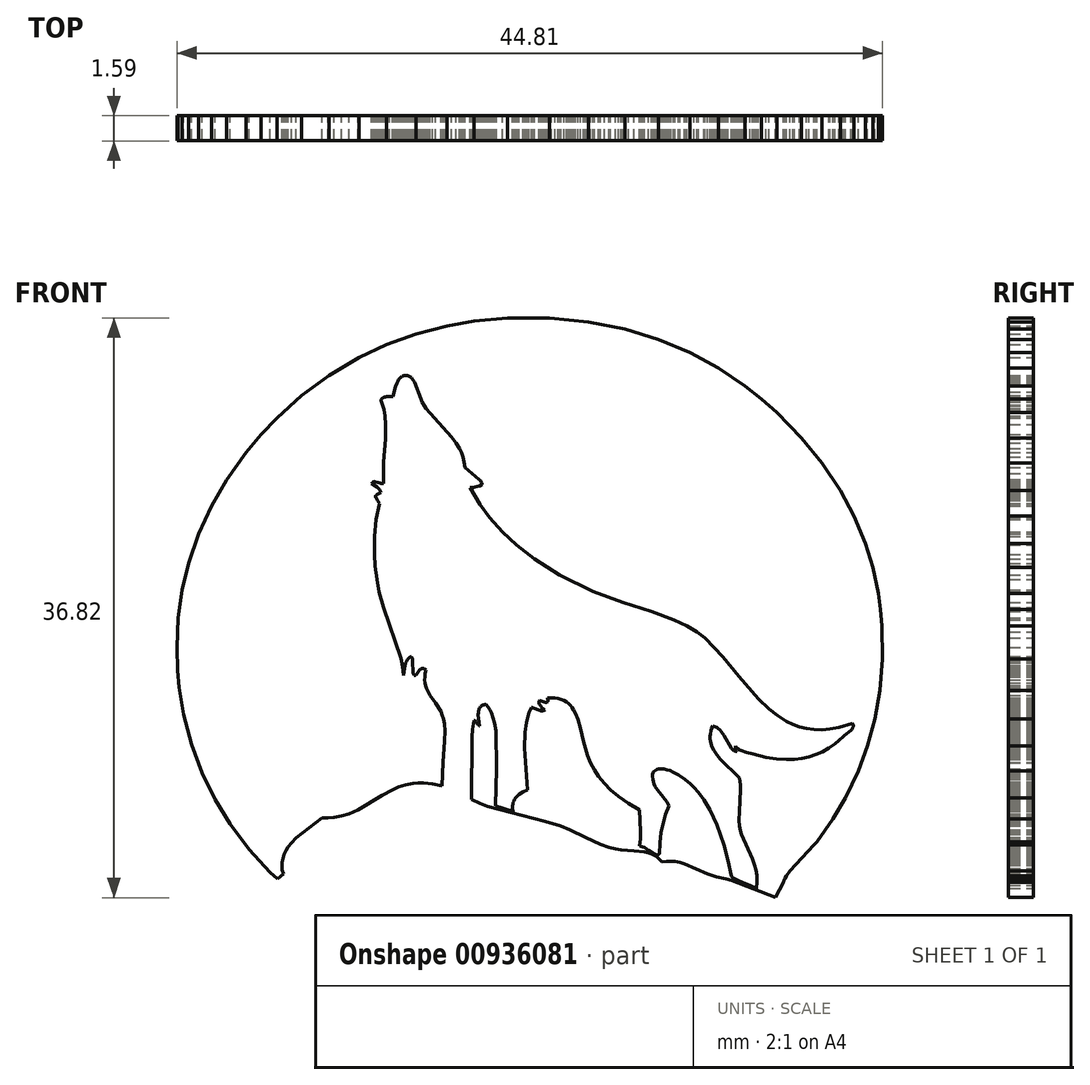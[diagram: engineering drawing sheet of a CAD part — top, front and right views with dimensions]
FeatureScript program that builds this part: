
annotation { "Feature Type Name" : "Feature", "Feature Type Description" : "" }
export const myFeature = defineFeature(function(context is Context, id is Id, definition is map)
    precondition{}
    {
        {
            var Q0;
            Q0=qCreatedBy(makeId("Front.planeOp"),FACE);
            var sketch = newSketch(context, id + "F0", { "sketchPlane" : qUnion([Q0])});
            skLineSegment(sketch, "E0", {"start": v(-25.4, -24.26) * mm, "end": v(-25.3, -24.48) * mm});
            skLineSegment(sketch, "E1", {"start": v(-25.3, -24.48) * mm, "end": v(-25.21, -24.65) * mm});
            skLineSegment(sketch, "E2", {"start": v(-25.21, -24.65) * mm, "end": v(-25.12, -24.8) * mm});
            skLineSegment(sketch, "E3", {"start": v(-25.12, -24.8) * mm, "end": v(-25.03, -24.9) * mm});
            skLineSegment(sketch, "E4", {"start": v(-25.03, -24.9) * mm, "end": v(-24.93, -25) * mm});
            skLineSegment(sketch, "E5", {"start": v(-24.93, -25) * mm, "end": v(-24.82, -25.08) * mm});
            skLineSegment(sketch, "E6", {"start": v(-24.82, -25.08) * mm, "end": v(-24.7, -25.16) * mm});
            skLineSegment(sketch, "E7", {"start": v(-24.7, -25.16) * mm, "end": v(-24.6, -25.21) * mm});
            skLineSegment(sketch, "E8", {"start": v(-24.6, -25.21) * mm, "end": v(-24.47, -25.27) * mm});
            skLineSegment(sketch, "E9", {"start": v(-24.47, -25.27) * mm, "end": v(-14.22, -25.27) * mm});
            skLineSegment(sketch, "E10", {"start": v(-14.22, -25.27) * mm, "end": v(-16.34, -23.58) * mm});
            skLineSegment(sketch, "E11", {"start": v(-16.34, -23.58) * mm, "end": v(-17.75, -22.6) * mm});
            skLineSegment(sketch, "E12", {"start": v(-17.75, -22.6) * mm, "end": v(-17.95, -22.4) * mm});
            skLineSegment(sketch, "E13", {"start": v(-17.95, -22.4) * mm, "end": v(-18.06, -22.27) * mm});
            skLineSegment(sketch, "E14", {"start": v(-18.06, -22.27) * mm, "end": v(-18.14, -22.14) * mm});
            skLineSegment(sketch, "E15", {"start": v(-18.14, -22.14) * mm, "end": v(-18.21, -22) * mm});
            skLineSegment(sketch, "E16", {"start": v(-18.21, -22) * mm, "end": v(-18.25, -21.91) * mm});
            skLineSegment(sketch, "E17", {"start": v(-18.25, -21.91) * mm, "end": v(-18.27, -21.82) * mm});
            skLineSegment(sketch, "E18", {"start": v(-18.27, -21.82) * mm, "end": v(-18.29, -21.72) * mm});
            skLineSegment(sketch, "E19", {"start": v(-18.29, -21.72) * mm, "end": v(-18.3, -21.66) * mm});
            skLineSegment(sketch, "E20", {"start": v(-18.3, -21.66) * mm, "end": v(-18.29, -21.58) * mm});
            skLineSegment(sketch, "E21", {"start": v(-18.29, -21.58) * mm, "end": v(-18.27, -21.49) * mm});
            skLineSegment(sketch, "E22", {"start": v(-18.27, -21.49) * mm, "end": v(-18.23, -21.33) * mm});
            skLineSegment(sketch, "E23", {"start": v(-18.23, -21.33) * mm, "end": v(-17.9, -20.37) * mm});
            skLineSegment(sketch, "E24", {"start": v(-17.9, -20.37) * mm, "end": v(-17.87, -20.24) * mm});
            skLineSegment(sketch, "E25", {"start": v(-17.87, -20.24) * mm, "end": v(-17.87, -20.17) * mm});
            skLineSegment(sketch, "E26", {"start": v(-17.87, -20.17) * mm, "end": v(-17.86, -20.1) * mm});
            skLineSegment(sketch, "E27", {"start": v(-17.86, -20.1) * mm, "end": v(-17.87, -20.02) * mm});
            skLineSegment(sketch, "E28", {"start": v(-17.87, -20.02) * mm, "end": v(-17.9, -19.9) * mm});
            skLineSegment(sketch, "E29", {"start": v(-17.9, -19.9) * mm, "end": v(-17.93, -19.76) * mm});
            skLineSegment(sketch, "E30", {"start": v(-17.93, -19.76) * mm, "end": v(-18, -19.6) * mm});
            skLineSegment(sketch, "E31", {"start": v(-18, -19.6) * mm, "end": v(-18.16, -19.28) * mm});
            skLineSegment(sketch, "E32", {"start": v(-18.16, -19.28) * mm, "end": v(-18.57, -18.53) * mm});
            skLineSegment(sketch, "E33", {"start": v(-18.57, -18.53) * mm, "end": v(-18.64, -18.35) * mm});
            skLineSegment(sketch, "E34", {"start": v(-18.64, -18.35) * mm, "end": v(-18.68, -18.22) * mm});
            skLineSegment(sketch, "E35", {"start": v(-18.68, -18.22) * mm, "end": v(-18.7, -18.08) * mm});
            skLineSegment(sketch, "E36", {"start": v(-18.7, -18.08) * mm, "end": v(-18.71, -18) * mm});
            skLineSegment(sketch, "E37", {"start": v(-18.71, -18) * mm, "end": v(-18.71, -17.9) * mm});
            skLineSegment(sketch, "E38", {"start": v(-18.71, -17.9) * mm, "end": v(-18.7, -17.78) * mm});
            skLineSegment(sketch, "E39", {"start": v(-18.7, -17.78) * mm, "end": v(-18.66, -17.65) * mm});
            skLineSegment(sketch, "E40", {"start": v(-18.66, -17.65) * mm, "end": v(-18.6, -17.54) * mm});
            skLineSegment(sketch, "E41", {"start": v(-18.6, -17.54) * mm, "end": v(-18.54, -17.42) * mm});
            skLineSegment(sketch, "E42", {"start": v(-18.54, -17.42) * mm, "end": v(-18.46, -17.31) * mm});
            skLineSegment(sketch, "E43", {"start": v(-18.46, -17.31) * mm, "end": v(-18.32, -17.15) * mm});
            skLineSegment(sketch, "E44", {"start": v(-18.32, -17.15) * mm, "end": v(-18.1, -16.95) * mm});
            skLineSegment(sketch, "E45", {"start": v(-18.1, -16.95) * mm, "end": v(-17.67, -16.63) * mm});
            skLineSegment(sketch, "E46", {"start": v(-17.67, -16.63) * mm, "end": v(-16.85, -16.04) * mm});
            skLineSegment(sketch, "E47", {"start": v(-16.85, -16.04) * mm, "end": v(-16.72, -15.92) * mm});
            skLineSegment(sketch, "E48", {"start": v(-16.72, -15.92) * mm, "end": v(-16.64, -15.84) * mm});
            skLineSegment(sketch, "E49", {"start": v(-16.64, -15.84) * mm, "end": v(-16.59, -15.75) * mm});
            skLineSegment(sketch, "E50", {"start": v(-16.59, -15.75) * mm, "end": v(-16.54, -15.67) * mm});
            skLineSegment(sketch, "E51", {"start": v(-16.54, -15.67) * mm, "end": v(-16.53, -15.62) * mm});
            skLineSegment(sketch, "E52", {"start": v(-16.53, -15.62) * mm, "end": v(-16.52, -15.58) * mm});
            skLineSegment(sketch, "E53", {"start": v(-16.52, -15.58) * mm, "end": v(-16.51, -15.54) * mm});
            skLineSegment(sketch, "E54", {"start": v(-16.51, -15.54) * mm, "end": v(-16.5, -15.5) * mm});
            skLineSegment(sketch, "E55", {"start": v(-16.5, -15.5) * mm, "end": v(-16.51, -15.48) * mm});
            skLineSegment(sketch, "E56", {"start": v(-16.51, -15.48) * mm, "end": v(-16.52, -15.43) * mm});
            skLineSegment(sketch, "E57", {"start": v(-16.52, -15.43) * mm, "end": v(-16.54, -15.37) * mm});
            skLineSegment(sketch, "E58", {"start": v(-16.54, -15.37) * mm, "end": v(-16.57, -15.3) * mm});
            skLineSegment(sketch, "E59", {"start": v(-16.57, -15.3) * mm, "end": v(-16.62, -15.21) * mm});
            skLineSegment(sketch, "E60", {"start": v(-16.62, -15.21) * mm, "end": v(-16.72, -15.08) * mm});
            skLineSegment(sketch, "E61", {"start": v(-16.72, -15.08) * mm, "end": v(-16.9, -14.88) * mm});
            skLineSegment(sketch, "E62", {"start": v(-16.9, -14.88) * mm, "end": v(-17.4, -14.42) * mm});
            skLineSegment(sketch, "E63", {"start": v(-17.4, -14.42) * mm, "end": v(-17.86, -14.01) * mm});
            skLineSegment(sketch, "E64", {"start": v(-17.86, -14.01) * mm, "end": v(-19.2, -12.55) * mm});
            skLineSegment(sketch, "E65", {"start": v(-19.2, -12.55) * mm, "end": v(-20.43, -10.91) * mm});
            skLineSegment(sketch, "E66", {"start": v(-20.43, -10.91) * mm, "end": v(-21.37, -9.37) * mm});
            skLineSegment(sketch, "E67", {"start": v(-21.37, -9.37) * mm, "end": v(-22.2, -7.7) * mm});
            skLineSegment(sketch, "E68", {"start": v(-22.2, -7.7) * mm, "end": v(-22.87, -5.9) * mm});
            skLineSegment(sketch, "E69", {"start": v(-22.87, -5.9) * mm, "end": v(-23.37, -3.96) * mm});
            skLineSegment(sketch, "E70", {"start": v(-23.37, -3.96) * mm, "end": v(-23.65, -2.25) * mm});
            skLineSegment(sketch, "E71", {"start": v(-23.65, -2.25) * mm, "end": v(-23.75, -1.18) * mm});
            skLineSegment(sketch, "E72", {"start": v(-23.75, -1.18) * mm, "end": v(-23.8, 0.3) * mm});
            skLineSegment(sketch, "E73", {"start": v(-23.8, 0.3) * mm, "end": v(-23.7, 2.16) * mm});
            skLineSegment(sketch, "E74", {"start": v(-23.7, 2.16) * mm, "end": v(-23.44, 3.93) * mm});
            skLineSegment(sketch, "E75", {"start": v(-23.44, 3.93) * mm, "end": v(-23.04, 5.6) * mm});
            skLineSegment(sketch, "E76", {"start": v(-23.04, 5.6) * mm, "end": v(-22.4, 7.5) * mm});
            skLineSegment(sketch, "E77", {"start": v(-22.4, 7.5) * mm, "end": v(-21.58, 9.27) * mm});
            skLineSegment(sketch, "E78", {"start": v(-21.58, 9.27) * mm, "end": v(-20.64, 10.9) * mm});
            skLineSegment(sketch, "E79", {"start": v(-20.64, 10.9) * mm, "end": v(-19.4, 12.66) * mm});
            skLineSegment(sketch, "E80", {"start": v(-19.4, 12.66) * mm, "end": v(-18.44, 13.8) * mm});
            skLineSegment(sketch, "E81", {"start": v(-18.44, 13.8) * mm, "end": v(-17.44, 14.86) * mm});
            skLineSegment(sketch, "E82", {"start": v(-17.44, 14.86) * mm, "end": v(-15.87, 16.28) * mm});
            skLineSegment(sketch, "E83", {"start": v(-15.87, 16.28) * mm, "end": v(-14.13, 17.56) * mm});
            skLineSegment(sketch, "E84", {"start": v(-14.13, 17.56) * mm, "end": v(-12.22, 18.69) * mm});
            skLineSegment(sketch, "E85", {"start": v(-12.22, 18.69) * mm, "end": v(-10.46, 19.51) * mm});
            skLineSegment(sketch, "E86", {"start": v(-10.46, 19.51) * mm, "end": v(-8.6, 20.2) * mm});
            skLineSegment(sketch, "E87", {"start": v(-8.6, 20.2) * mm, "end": v(-6.63, 20.71) * mm});
            skLineSegment(sketch, "E88", {"start": v(-6.63, 20.71) * mm, "end": v(-4.92, 21.02) * mm});
            skLineSegment(sketch, "E89", {"start": v(-4.92, 21.02) * mm, "end": v(-2.8, 21.2) * mm});
            skLineSegment(sketch, "E90", {"start": v(-2.8, 21.2) * mm, "end": v(-0.13, 21.2) * mm});
            skLineSegment(sketch, "E91", {"start": v(-0.13, 21.2) * mm, "end": v(2.36, 20.96) * mm});
            skLineSegment(sketch, "E92", {"start": v(2.36, 20.96) * mm, "end": v(4.67, 20.5) * mm});
            skLineSegment(sketch, "E93", {"start": v(4.67, 20.5) * mm, "end": v(6.81, 19.85) * mm});
            skLineSegment(sketch, "E94", {"start": v(6.81, 19.85) * mm, "end": v(8.79, 19.01) * mm});
            skLineSegment(sketch, "E95", {"start": v(8.79, 19.01) * mm, "end": v(10.61, 18.02) * mm});
            skLineSegment(sketch, "E96", {"start": v(10.61, 18.02) * mm, "end": v(12.3, 16.89) * mm});
            skLineSegment(sketch, "E97", {"start": v(12.3, 16.89) * mm, "end": v(13.33, 16.07) * mm});
            skLineSegment(sketch, "E98", {"start": v(13.33, 16.07) * mm, "end": v(14.3, 15.2) * mm});
            skLineSegment(sketch, "E99", {"start": v(14.3, 15.2) * mm, "end": v(15.89, 13.58) * mm});
            skLineSegment(sketch, "E100", {"start": v(15.89, 13.58) * mm, "end": v(17.18, 12) * mm});
            skLineSegment(sketch, "E101", {"start": v(17.18, 12) * mm, "end": v(18.34, 10.26) * mm});
            skLineSegment(sketch, "E102", {"start": v(18.34, 10.26) * mm, "end": v(19.21, 8.64) * mm});
            skLineSegment(sketch, "E103", {"start": v(19.21, 8.64) * mm, "end": v(19.94, 6.9) * mm});
            skLineSegment(sketch, "E104", {"start": v(19.94, 6.9) * mm, "end": v(20.42, 5.36) * mm});
            skLineSegment(sketch, "E105", {"start": v(20.42, 5.36) * mm, "end": v(20.77, 3.73) * mm});
            skLineSegment(sketch, "E106", {"start": v(20.77, 3.73) * mm, "end": v(20.9, 2.7) * mm});
            skLineSegment(sketch, "E107", {"start": v(20.9, 2.7) * mm, "end": v(21, 1.65) * mm});
            skLineSegment(sketch, "E108", {"start": v(21, 1.65) * mm, "end": v(21.02, -0.46) * mm});
            skLineSegment(sketch, "E109", {"start": v(21.02, -0.46) * mm, "end": v(20.87, -2.43) * mm});
            skLineSegment(sketch, "E110", {"start": v(20.87, -2.43) * mm, "end": v(20.55, -4.27) * mm});
            skLineSegment(sketch, "E111", {"start": v(20.55, -4.27) * mm, "end": v(20.09, -5.98) * mm});
            skLineSegment(sketch, "E112", {"start": v(20.09, -5.98) * mm, "end": v(19.5, -7.57) * mm});
            skLineSegment(sketch, "E113", {"start": v(19.5, -7.57) * mm, "end": v(18.67, -9.27) * mm});
            skLineSegment(sketch, "E114", {"start": v(18.67, -9.27) * mm, "end": v(17.87, -10.62) * mm});
            skLineSegment(sketch, "E115", {"start": v(17.87, -10.62) * mm, "end": v(16.85, -12.07) * mm});
            skLineSegment(sketch, "E116", {"start": v(16.85, -12.07) * mm, "end": v(16.67, -12.27) * mm});
            skLineSegment(sketch, "E117", {"start": v(16.67, -12.27) * mm, "end": v(15.14, -13.9) * mm});
            skLineSegment(sketch, "E118", {"start": v(15.14, -13.9) * mm, "end": v(14.92, -14.21) * mm});
            skLineSegment(sketch, "E119", {"start": v(14.92, -14.21) * mm, "end": v(14.82, -14.4) * mm});
            skLineSegment(sketch, "E120", {"start": v(14.82, -14.4) * mm, "end": v(14.77, -14.52) * mm});
            skLineSegment(sketch, "E121", {"start": v(14.77, -14.52) * mm, "end": v(14.74, -14.63) * mm});
            skLineSegment(sketch, "E122", {"start": v(14.74, -14.63) * mm, "end": v(14.72, -14.74) * mm});
            skLineSegment(sketch, "E123", {"start": v(14.72, -14.74) * mm, "end": v(14.72, -14.85) * mm});
            skLineSegment(sketch, "E124", {"start": v(14.72, -14.85) * mm, "end": v(14.72, -14.9) * mm});
            skLineSegment(sketch, "E125", {"start": v(14.72, -14.9) * mm, "end": v(14.73, -14.94) * mm});
            skLineSegment(sketch, "E126", {"start": v(14.73, -14.94) * mm, "end": v(14.74, -14.98) * mm});
            skLineSegment(sketch, "E127", {"start": v(14.74, -14.98) * mm, "end": v(14.76, -15) * mm});
            skLineSegment(sketch, "E128", {"start": v(14.76, -15) * mm, "end": v(14.8, -15.07) * mm});
            skLineSegment(sketch, "E129", {"start": v(14.8, -15.07) * mm, "end": v(14.84, -15.12) * mm});
            skLineSegment(sketch, "E130", {"start": v(14.84, -15.12) * mm, "end": v(14.9, -15.17) * mm});
            skLineSegment(sketch, "E131", {"start": v(14.9, -15.17) * mm, "end": v(14.96, -15.23) * mm});
            skLineSegment(sketch, "E132", {"start": v(14.96, -15.23) * mm, "end": v(15.08, -15.3) * mm});
            skLineSegment(sketch, "E133", {"start": v(15.08, -15.3) * mm, "end": v(15.26, -15.39) * mm});
            skLineSegment(sketch, "E134", {"start": v(15.26, -15.39) * mm, "end": v(16.16, -15.66) * mm});
            skLineSegment(sketch, "E135", {"start": v(16.16, -15.66) * mm, "end": v(17.02, -15.88) * mm});
            skLineSegment(sketch, "E136", {"start": v(17.02, -15.88) * mm, "end": v(18.6, -16.34) * mm});
            skLineSegment(sketch, "E137", {"start": v(18.6, -16.34) * mm, "end": v(18.9, -16.48) * mm});
            skLineSegment(sketch, "E138", {"start": v(18.9, -16.48) * mm, "end": v(19.1, -16.6) * mm});
            skLineSegment(sketch, "E139", {"start": v(19.1, -16.6) * mm, "end": v(19.25, -16.7) * mm});
            skLineSegment(sketch, "E140", {"start": v(19.25, -16.7) * mm, "end": v(19.39, -16.8) * mm});
            skLineSegment(sketch, "E141", {"start": v(19.39, -16.8) * mm, "end": v(18.26, -16.72) * mm});
            skLineSegment(sketch, "E142", {"start": v(18.26, -16.72) * mm, "end": v(17.04, -16.51) * mm});
            skLineSegment(sketch, "E143", {"start": v(17.04, -16.51) * mm, "end": v(14.22, -15.6) * mm});
            skLineSegment(sketch, "E144", {"start": v(14.22, -15.6) * mm, "end": v(11.43, -14.52) * mm});
            skLineSegment(sketch, "E145", {"start": v(11.43, -14.52) * mm, "end": v(11.07, -14.42) * mm});
            skLineSegment(sketch, "E146", {"start": v(11.07, -14.42) * mm, "end": v(10.48, -14.28) * mm});
            skLineSegment(sketch, "E147", {"start": v(10.48, -14.28) * mm, "end": v(9.9, -14.1) * mm});
            skLineSegment(sketch, "E148", {"start": v(9.9, -14.1) * mm, "end": v(8.46, -13.45) * mm});
            skLineSegment(sketch, "E149", {"start": v(8.46, -13.45) * mm, "end": v(8.17, -13.37) * mm});
            skLineSegment(sketch, "E150", {"start": v(8.17, -13.37) * mm, "end": v(7.86, -13.32) * mm});
            skLineSegment(sketch, "E151", {"start": v(7.86, -13.32) * mm, "end": v(7.6, -13.3) * mm});
            skLineSegment(sketch, "E152", {"start": v(7.6, -13.3) * mm, "end": v(7.32, -13.3) * mm});
            skLineSegment(sketch, "E153", {"start": v(7.32, -13.3) * mm, "end": v(7.03, -13.34) * mm});
            skLineSegment(sketch, "E154", {"start": v(7.03, -13.34) * mm, "end": v(6.87, -13.16) * mm});
            skLineSegment(sketch, "E155", {"start": v(6.87, -13.16) * mm, "end": v(6.74, -13.06) * mm});
            skLineSegment(sketch, "E156", {"start": v(6.74, -13.06) * mm, "end": v(6.61, -12.97) * mm});
            skLineSegment(sketch, "E157", {"start": v(6.61, -12.97) * mm, "end": v(6.48, -12.9) * mm});
            skLineSegment(sketch, "E158", {"start": v(6.48, -12.9) * mm, "end": v(6.35, -12.83) * mm});
            skLineSegment(sketch, "E159", {"start": v(6.35, -12.83) * mm, "end": v(6.16, -12.76) * mm});
            skLineSegment(sketch, "E160", {"start": v(6.16, -12.76) * mm, "end": v(5.92, -12.7) * mm});
            skLineSegment(sketch, "E161", {"start": v(5.92, -12.7) * mm, "end": v(5.26, -12.64) * mm});
            skLineSegment(sketch, "E162", {"start": v(5.26, -12.64) * mm, "end": v(4.4, -12.57) * mm});
            skLineSegment(sketch, "E163", {"start": v(4.4, -12.57) * mm, "end": v(4.06, -12.52) * mm});
            skLineSegment(sketch, "E164", {"start": v(4.06, -12.52) * mm, "end": v(3.66, -12.42) * mm});
            skLineSegment(sketch, "E165", {"start": v(3.66, -12.42) * mm, "end": v(3.13, -12.23) * mm});
            skLineSegment(sketch, "E166", {"start": v(3.13, -12.23) * mm, "end": v(2.17, -11.8) * mm});
            skLineSegment(sketch, "E167", {"start": v(2.17, -11.8) * mm, "end": v(1.18, -11.3) * mm});
            skLineSegment(sketch, "E168", {"start": v(1.18, -11.3) * mm, "end": v(0.6, -11.06) * mm});
            skLineSegment(sketch, "E169", {"start": v(0.6, -11.06) * mm, "end": v(-0.42, -10.75) * mm});
            skLineSegment(sketch, "E170", {"start": v(-0.42, -10.75) * mm, "end": v(-4.07, -9.82) * mm});
            skLineSegment(sketch, "E171", {"start": v(-4.07, -9.82) * mm, "end": v(-4.54, -9.63) * mm});
            skLineSegment(sketch, "E172", {"start": v(-4.54, -9.63) * mm, "end": v(-5.08, -9.36) * mm});
            skLineSegment(sketch, "E173", {"start": v(-5.08, -9.36) * mm, "end": v(-5.06, -5.4) * mm});
            skLineSegment(sketch, "E174", {"start": v(-5.06, -5.4) * mm, "end": v(-5, -4.91) * mm});
            skLineSegment(sketch, "E175", {"start": v(-5, -4.91) * mm, "end": v(-4.91, -4.36) * mm});
            skLineSegment(sketch, "E176", {"start": v(-4.91, -4.36) * mm, "end": v(-4.89, -4.36) * mm});
            skLineSegment(sketch, "E177", {"start": v(-4.89, -4.36) * mm, "end": v(-4.87, -4.37) * mm});
            skLineSegment(sketch, "E178", {"start": v(-4.87, -4.37) * mm, "end": v(-4.85, -4.38) * mm});
            skLineSegment(sketch, "E179", {"start": v(-4.85, -4.38) * mm, "end": v(-4.83, -4.39) * mm});
            skLineSegment(sketch, "E180", {"start": v(-4.83, -4.39) * mm, "end": v(-4.81, -4.4) * mm});
            skLineSegment(sketch, "E181", {"start": v(-4.81, -4.4) * mm, "end": v(-4.8, -4.41) * mm});
            skLineSegment(sketch, "E182", {"start": v(-4.8, -4.41) * mm, "end": v(-4.78, -4.43) * mm});
            skLineSegment(sketch, "E183", {"start": v(-4.78, -4.43) * mm, "end": v(-4.76, -4.45) * mm});
            skLineSegment(sketch, "E184", {"start": v(-4.76, -4.45) * mm, "end": v(-4.73, -4.5) * mm});
            skLineSegment(sketch, "E185", {"start": v(-4.73, -4.5) * mm, "end": v(-4.65, -4.63) * mm});
            skLineSegment(sketch, "E186", {"start": v(-4.65, -4.63) * mm, "end": v(-4.63, -4.65) * mm});
            skLineSegment(sketch, "E187", {"start": v(-4.63, -4.65) * mm, "end": v(-4.61, -4.67) * mm});
            skLineSegment(sketch, "E188", {"start": v(-4.61, -4.67) * mm, "end": v(-4.6, -4.68) * mm});
            skLineSegment(sketch, "E189", {"start": v(-4.6, -4.68) * mm, "end": v(-4.59, -4.69) * mm});
            skLineSegment(sketch, "E190", {"start": v(-4.59, -4.69) * mm, "end": v(-4.57, -4.7) * mm});
            skLineSegment(sketch, "E191", {"start": v(-4.57, -4.7) * mm, "end": v(-4.64, -4.21) * mm});
            skLineSegment(sketch, "E192", {"start": v(-4.64, -4.21) * mm, "end": v(-4.65, -4) * mm});
            skLineSegment(sketch, "E193", {"start": v(-4.65, -4) * mm, "end": v(-4.65, -3.86) * mm});
            skLineSegment(sketch, "E194", {"start": v(-4.65, -3.86) * mm, "end": v(-4.63, -3.76) * mm});
            skLineSegment(sketch, "E195", {"start": v(-4.63, -3.76) * mm, "end": v(-4.6, -3.67) * mm});
            skLineSegment(sketch, "E196", {"start": v(-4.6, -3.67) * mm, "end": v(-4.59, -3.61) * mm});
            skLineSegment(sketch, "E197", {"start": v(-4.59, -3.61) * mm, "end": v(-4.56, -3.56) * mm});
            skLineSegment(sketch, "E198", {"start": v(-4.56, -3.56) * mm, "end": v(-4.53, -3.52) * mm});
            skLineSegment(sketch, "E199", {"start": v(-4.53, -3.52) * mm, "end": v(-4.5, -3.47) * mm});
            skLineSegment(sketch, "E200", {"start": v(-4.5, -3.47) * mm, "end": v(-4.45, -3.44) * mm});
            skLineSegment(sketch, "E201", {"start": v(-4.45, -3.44) * mm, "end": v(-4.4, -3.4) * mm});
            skLineSegment(sketch, "E202", {"start": v(-4.4, -3.4) * mm, "end": v(-4.35, -3.38) * mm});
            skLineSegment(sketch, "E203", {"start": v(-4.35, -3.38) * mm, "end": v(-4.3, -3.36) * mm});
            skLineSegment(sketch, "E204", {"start": v(-4.3, -3.36) * mm, "end": v(-4.22, -3.35) * mm});
            skLineSegment(sketch, "E205", {"start": v(-4.22, -3.35) * mm, "end": v(-4.15, -3.34) * mm});
            skLineSegment(sketch, "E206", {"start": v(-4.15, -3.34) * mm, "end": v(-4.02, -3.5) * mm});
            skLineSegment(sketch, "E207", {"start": v(-4.02, -3.5) * mm, "end": v(-3.92, -3.68) * mm});
            skLineSegment(sketch, "E208", {"start": v(-3.92, -3.68) * mm, "end": v(-3.82, -3.87) * mm});
            skLineSegment(sketch, "E209", {"start": v(-3.82, -3.87) * mm, "end": v(-3.7, -4.18) * mm});
            skLineSegment(sketch, "E210", {"start": v(-3.7, -4.18) * mm, "end": v(-3.6, -4.52) * mm});
            skLineSegment(sketch, "E211", {"start": v(-3.6, -4.52) * mm, "end": v(-3.52, -5.02) * mm});
            skLineSegment(sketch, "E212", {"start": v(-3.52, -5.02) * mm, "end": v(-3.47, -7.43) * mm});
            skLineSegment(sketch, "E213", {"start": v(-3.47, -7.43) * mm, "end": v(-3.56, -9.78) * mm});
            skLineSegment(sketch, "E214", {"start": v(-3.56, -9.78) * mm, "end": v(-2.46, -10.12) * mm});
            skLineSegment(sketch, "E215", {"start": v(-2.46, -10.12) * mm, "end": v(-2.47, -9.92) * mm});
            skLineSegment(sketch, "E216", {"start": v(-2.47, -9.92) * mm, "end": v(-2.47, -9.78) * mm});
            skLineSegment(sketch, "E217", {"start": v(-2.47, -9.78) * mm, "end": v(-2.45, -9.66) * mm});
            skLineSegment(sketch, "E218", {"start": v(-2.45, -9.66) * mm, "end": v(-2.43, -9.55) * mm});
            skLineSegment(sketch, "E219", {"start": v(-2.43, -9.55) * mm, "end": v(-2.39, -9.45) * mm});
            skLineSegment(sketch, "E220", {"start": v(-2.39, -9.45) * mm, "end": v(-2.34, -9.36) * mm});
            skLineSegment(sketch, "E221", {"start": v(-2.34, -9.36) * mm, "end": v(-2.28, -9.28) * mm});
            skLineSegment(sketch, "E222", {"start": v(-2.28, -9.28) * mm, "end": v(-2.22, -9.21) * mm});
            skLineSegment(sketch, "E223", {"start": v(-2.22, -9.21) * mm, "end": v(-2.15, -9.14) * mm});
            skLineSegment(sketch, "E224", {"start": v(-2.15, -9.14) * mm, "end": v(-2.05, -9.06) * mm});
            skLineSegment(sketch, "E225", {"start": v(-2.05, -9.06) * mm, "end": v(-1.8, -8.9) * mm});
            skLineSegment(sketch, "E226", {"start": v(-1.8, -8.9) * mm, "end": v(-1.52, -8.76) * mm});
            skLineSegment(sketch, "E227", {"start": v(-1.52, -8.76) * mm, "end": v(-1.7, -6.11) * mm});
            skLineSegment(sketch, "E228", {"start": v(-1.7, -6.11) * mm, "end": v(-1.67, -5.1) * mm});
            skLineSegment(sketch, "E229", {"start": v(-1.67, -5.1) * mm, "end": v(-1.59, -4.48) * mm});
            skLineSegment(sketch, "E230", {"start": v(-1.59, -4.48) * mm, "end": v(-1.5, -4.1) * mm});
            skLineSegment(sketch, "E231", {"start": v(-1.5, -4.1) * mm, "end": v(-1.41, -3.83) * mm});
            skLineSegment(sketch, "E232", {"start": v(-1.41, -3.83) * mm, "end": v(-1.27, -3.51) * mm});
            skLineSegment(sketch, "E233", {"start": v(-1.27, -3.51) * mm, "end": v(-1.22, -3.52) * mm});
            skLineSegment(sketch, "E234", {"start": v(-1.22, -3.52) * mm, "end": v(-1.16, -3.55) * mm});
            skLineSegment(sketch, "E235", {"start": v(-1.16, -3.55) * mm, "end": v(-0.72, -3.73) * mm});
            skLineSegment(sketch, "E236", {"start": v(-0.72, -3.73) * mm, "end": v(-0.67, -3.74) * mm});
            skLineSegment(sketch, "E237", {"start": v(-0.67, -3.74) * mm, "end": v(-0.62, -3.75) * mm});
            skLineSegment(sketch, "E238", {"start": v(-0.62, -3.75) * mm, "end": v(-0.58, -3.75) * mm});
            skLineSegment(sketch, "E239", {"start": v(-0.58, -3.75) * mm, "end": v(-0.55, -3.75) * mm});
            skLineSegment(sketch, "E240", {"start": v(-0.55, -3.75) * mm, "end": v(-0.52, -3.74) * mm});
            skLineSegment(sketch, "E241", {"start": v(-0.52, -3.74) * mm, "end": v(-0.5, -3.73) * mm});
            skLineSegment(sketch, "E242", {"start": v(-0.5, -3.73) * mm, "end": v(-0.46, -3.71) * mm});
            skLineSegment(sketch, "E243", {"start": v(-0.46, -3.71) * mm, "end": v(-0.45, -3.7) * mm});
            skLineSegment(sketch, "E244", {"start": v(-0.45, -3.7) * mm, "end": v(-0.42, -3.68) * mm});
            skLineSegment(sketch, "E245", {"start": v(-0.42, -3.68) * mm, "end": v(-0.45, -3.67) * mm});
            skLineSegment(sketch, "E246", {"start": v(-0.45, -3.67) * mm, "end": v(-0.47, -3.66) * mm});
            skLineSegment(sketch, "E247", {"start": v(-0.47, -3.66) * mm, "end": v(-0.5, -3.64) * mm});
            skLineSegment(sketch, "E248", {"start": v(-0.5, -3.64) * mm, "end": v(-0.56, -3.6) * mm});
            skLineSegment(sketch, "E249", {"start": v(-0.56, -3.6) * mm, "end": v(-0.6, -3.54) * mm});
            skLineSegment(sketch, "E250", {"start": v(-0.6, -3.54) * mm, "end": v(-0.66, -3.47) * mm});
            skLineSegment(sketch, "E251", {"start": v(-0.66, -3.47) * mm, "end": v(-0.7, -3.4) * mm});
            skLineSegment(sketch, "E252", {"start": v(-0.7, -3.4) * mm, "end": v(-0.75, -3.32) * mm});
            skLineSegment(sketch, "E253", {"start": v(-0.75, -3.32) * mm, "end": v(-0.77, -3.26) * mm});
            skLineSegment(sketch, "E254", {"start": v(-0.77, -3.26) * mm, "end": v(-0.79, -3.22) * mm});
            skLineSegment(sketch, "E255", {"start": v(-0.79, -3.22) * mm, "end": v(-0.8, -3.2) * mm});
            skLineSegment(sketch, "E256", {"start": v(-0.8, -3.2) * mm, "end": v(-0.8, -3.17) * mm});
            skLineSegment(sketch, "E257", {"start": v(-0.8, -3.17) * mm, "end": v(-0.8, -3.15) * mm});
            skLineSegment(sketch, "E258", {"start": v(-0.8, -3.15) * mm, "end": v(-0.79, -3.13) * mm});
            skLineSegment(sketch, "E259", {"start": v(-0.79, -3.13) * mm, "end": v(-0.78, -3.12) * mm});
            skLineSegment(sketch, "E260", {"start": v(-0.78, -3.12) * mm, "end": v(-0.78, -3.11) * mm});
            skLineSegment(sketch, "E261", {"start": v(-0.78, -3.11) * mm, "end": v(-0.77, -3.1) * mm});
            skLineSegment(sketch, "E262", {"start": v(-0.77, -3.1) * mm, "end": v(-0.77, -3.1) * mm});
            skLineSegment(sketch, "E263", {"start": v(-0.77, -3.1) * mm, "end": v(-0.76, -3.1) * mm});
            skLineSegment(sketch, "E264", {"start": v(-0.76, -3.1) * mm, "end": v(-0.47, -3.19) * mm});
            skLineSegment(sketch, "E265", {"start": v(-0.47, -3.19) * mm, "end": v(-0.39, -3.2) * mm});
            skLineSegment(sketch, "E266", {"start": v(-0.39, -3.2) * mm, "end": v(-0.34, -3.21) * mm});
            skLineSegment(sketch, "E267", {"start": v(-0.34, -3.21) * mm, "end": v(-0.32, -3.2) * mm});
            skLineSegment(sketch, "E268", {"start": v(-0.32, -3.2) * mm, "end": v(-0.3, -3.2) * mm});
            skLineSegment(sketch, "E269", {"start": v(-0.3, -3.2) * mm, "end": v(-0.28, -3.2) * mm});
            skLineSegment(sketch, "E270", {"start": v(-0.28, -3.2) * mm, "end": v(-0.27, -3.2) * mm});
            skLineSegment(sketch, "E271", {"start": v(-0.27, -3.2) * mm, "end": v(-0.27, -3.2) * mm});
            skLineSegment(sketch, "E272", {"start": v(-0.27, -3.2) * mm, "end": v(-0.26, -3.19) * mm});
            skLineSegment(sketch, "E273", {"start": v(-0.26, -3.19) * mm, "end": v(-0.25, -3.18) * mm});
            skLineSegment(sketch, "E274", {"start": v(-0.25, -3.18) * mm, "end": v(-0.25, -3.18) * mm});
            skLineSegment(sketch, "E275", {"start": v(-0.25, -3.18) * mm, "end": v(-0.25, -3.17) * mm});
            skLineSegment(sketch, "E276", {"start": v(-0.25, -3.17) * mm, "end": v(-0.24, -3.16) * mm});
            skLineSegment(sketch, "E277", {"start": v(-0.24, -3.16) * mm, "end": v(-0.24, -3.15) * mm});
            skLineSegment(sketch, "E278", {"start": v(-0.24, -3.15) * mm, "end": v(-0.23, -3.13) * mm});
            skLineSegment(sketch, "E279", {"start": v(-0.23, -3.13) * mm, "end": v(-0.23, -3.11) * mm});
            skLineSegment(sketch, "E280", {"start": v(-0.23, -3.11) * mm, "end": v(-0.23, -3.09) * mm});
            skLineSegment(sketch, "E281", {"start": v(-0.23, -3.09) * mm, "end": v(-0.23, -3.05) * mm});
            skLineSegment(sketch, "E282", {"start": v(-0.23, -3.05) * mm, "end": v(-0.24, -3) * mm});
            skLineSegment(sketch, "E283", {"start": v(-0.24, -3) * mm, "end": v(-0.25, -2.92) * mm});
            skLineSegment(sketch, "E284", {"start": v(-0.25, -2.92) * mm, "end": v(0, -2.91) * mm});
            skLineSegment(sketch, "E285", {"start": v(0, -2.91) * mm, "end": v(0.22, -2.92) * mm});
            skLineSegment(sketch, "E286", {"start": v(0.22, -2.92) * mm, "end": v(0.43, -2.95) * mm});
            skLineSegment(sketch, "E287", {"start": v(0.43, -2.95) * mm, "end": v(0.62, -3) * mm});
            skLineSegment(sketch, "E288", {"start": v(0.62, -3) * mm, "end": v(0.79, -3.08) * mm});
            skLineSegment(sketch, "E289", {"start": v(0.79, -3.08) * mm, "end": v(0.94, -3.17) * mm});
            skLineSegment(sketch, "E290", {"start": v(0.94, -3.17) * mm, "end": v(1.08, -3.27) * mm});
            skLineSegment(sketch, "E291", {"start": v(1.08, -3.27) * mm, "end": v(1.2, -3.4) * mm});
            skLineSegment(sketch, "E292", {"start": v(1.2, -3.4) * mm, "end": v(1.32, -3.53) * mm});
            skLineSegment(sketch, "E293", {"start": v(1.32, -3.53) * mm, "end": v(1.41, -3.68) * mm});
            skLineSegment(sketch, "E294", {"start": v(1.41, -3.68) * mm, "end": v(1.54, -3.92) * mm});
            skLineSegment(sketch, "E295", {"start": v(1.54, -3.92) * mm, "end": v(1.68, -4.28) * mm});
            skLineSegment(sketch, "E296", {"start": v(1.68, -4.28) * mm, "end": v(1.85, -4.86) * mm});
            skLineSegment(sketch, "E297", {"start": v(1.85, -4.86) * mm, "end": v(2.04, -5.68) * mm});
            skLineSegment(sketch, "E298", {"start": v(2.04, -5.68) * mm, "end": v(2.29, -6.56) * mm});
            skLineSegment(sketch, "E299", {"start": v(2.29, -6.56) * mm, "end": v(2.5, -7.05) * mm});
            skLineSegment(sketch, "E300", {"start": v(2.5, -7.05) * mm, "end": v(2.73, -7.5) * mm});
            skLineSegment(sketch, "E301", {"start": v(2.73, -7.5) * mm, "end": v(3, -7.91) * mm});
            skLineSegment(sketch, "E302", {"start": v(3, -7.91) * mm, "end": v(3.36, -8.36) * mm});
            skLineSegment(sketch, "E303", {"start": v(3.36, -8.36) * mm, "end": v(3.76, -8.76) * mm});
            skLineSegment(sketch, "E304", {"start": v(3.76, -8.76) * mm, "end": v(4.27, -9.2) * mm});
            skLineSegment(sketch, "E305", {"start": v(4.27, -9.2) * mm, "end": v(4.9, -9.63) * mm});
            skLineSegment(sketch, "E306", {"start": v(4.9, -9.63) * mm, "end": v(5.59, -10.03) * mm});
            skLineSegment(sketch, "E307", {"start": v(5.59, -10.03) * mm, "end": v(5.67, -11.41) * mm});
            skLineSegment(sketch, "E308", {"start": v(5.67, -11.41) * mm, "end": v(5.65, -11.87) * mm});
            skLineSegment(sketch, "E309", {"start": v(5.65, -11.87) * mm, "end": v(5.59, -12.32) * mm});
            skLineSegment(sketch, "E310", {"start": v(5.59, -12.32) * mm, "end": v(5.64, -12.33) * mm});
            skLineSegment(sketch, "E311", {"start": v(5.64, -12.33) * mm, "end": v(5.7, -12.34) * mm});
            skLineSegment(sketch, "E312", {"start": v(5.7, -12.34) * mm, "end": v(5.78, -12.37) * mm});
            skLineSegment(sketch, "E313", {"start": v(5.78, -12.37) * mm, "end": v(5.9, -12.43) * mm});
            skLineSegment(sketch, "E314", {"start": v(5.9, -12.43) * mm, "end": v(6.17, -12.6) * mm});
            skLineSegment(sketch, "E315", {"start": v(6.17, -12.6) * mm, "end": v(6.53, -12.82) * mm});
            skLineSegment(sketch, "E316", {"start": v(6.53, -12.82) * mm, "end": v(6.6, -12.86) * mm});
            skLineSegment(sketch, "E317", {"start": v(6.6, -12.86) * mm, "end": v(6.65, -12.87) * mm});
            skLineSegment(sketch, "E318", {"start": v(6.65, -12.87) * mm, "end": v(6.69, -12.88) * mm});
            skLineSegment(sketch, "E319", {"start": v(6.69, -12.88) * mm, "end": v(6.73, -12.89) * mm});
            skLineSegment(sketch, "E320", {"start": v(6.73, -12.89) * mm, "end": v(6.75, -12.89) * mm});
            skLineSegment(sketch, "E321", {"start": v(6.75, -12.89) * mm, "end": v(6.77, -12.88) * mm});
            skLineSegment(sketch, "E322", {"start": v(6.77, -12.88) * mm, "end": v(6.78, -12.88) * mm});
            skLineSegment(sketch, "E323", {"start": v(6.78, -12.88) * mm, "end": v(6.8, -12.87) * mm});
            skLineSegment(sketch, "E324", {"start": v(6.8, -12.87) * mm, "end": v(6.82, -12.87) * mm});
            skLineSegment(sketch, "E325", {"start": v(6.82, -12.87) * mm, "end": v(6.83, -12.86) * mm});
            skLineSegment(sketch, "E326", {"start": v(6.83, -12.86) * mm, "end": v(6.84, -12.84) * mm});
            skLineSegment(sketch, "E327", {"start": v(6.84, -12.84) * mm, "end": v(6.86, -12.83) * mm});
            skLineSegment(sketch, "E328", {"start": v(6.86, -12.83) * mm, "end": v(6.88, -12.12) * mm});
            skLineSegment(sketch, "E329", {"start": v(6.88, -12.12) * mm, "end": v(6.96, -11.47) * mm});
            skLineSegment(sketch, "E330", {"start": v(6.96, -11.47) * mm, "end": v(7.1, -10.81) * mm});
            skLineSegment(sketch, "E331", {"start": v(7.1, -10.81) * mm, "end": v(7.25, -10.31) * mm});
            skLineSegment(sketch, "E332", {"start": v(7.25, -10.31) * mm, "end": v(7.45, -9.78) * mm});
            skLineSegment(sketch, "E333", {"start": v(7.45, -9.78) * mm, "end": v(7.4, -9.65) * mm});
            skLineSegment(sketch, "E334", {"start": v(7.4, -9.65) * mm, "end": v(7.33, -9.53) * mm});
            skLineSegment(sketch, "E335", {"start": v(7.33, -9.53) * mm, "end": v(7.22, -9.38) * mm});
            skLineSegment(sketch, "E336", {"start": v(7.22, -9.38) * mm, "end": v(6.64, -8.65) * mm});
            skLineSegment(sketch, "E337", {"start": v(6.64, -8.65) * mm, "end": v(6.57, -8.53) * mm});
            skLineSegment(sketch, "E338", {"start": v(6.57, -8.53) * mm, "end": v(6.51, -8.4) * mm});
            skLineSegment(sketch, "E339", {"start": v(6.51, -8.4) * mm, "end": v(6.47, -8.26) * mm});
            skLineSegment(sketch, "E340", {"start": v(6.47, -8.26) * mm, "end": v(6.44, -8.1) * mm});
            skLineSegment(sketch, "E341", {"start": v(6.44, -8.1) * mm, "end": v(6.42, -7.92) * mm});
            skLineSegment(sketch, "E342", {"start": v(6.42, -7.92) * mm, "end": v(6.43, -7.8) * mm});
            skLineSegment(sketch, "E343", {"start": v(6.43, -7.8) * mm, "end": v(6.43, -7.66) * mm});
            skLineSegment(sketch, "E344", {"start": v(6.43, -7.66) * mm, "end": v(6.52, -7.58) * mm});
            skLineSegment(sketch, "E345", {"start": v(6.52, -7.58) * mm, "end": v(6.6, -7.52) * mm});
            skLineSegment(sketch, "E346", {"start": v(6.6, -7.52) * mm, "end": v(6.7, -7.47) * mm});
            skLineSegment(sketch, "E347", {"start": v(6.7, -7.47) * mm, "end": v(6.8, -7.44) * mm});
            skLineSegment(sketch, "E348", {"start": v(6.8, -7.44) * mm, "end": v(6.91, -7.43) * mm});
            skLineSegment(sketch, "E349", {"start": v(6.91, -7.43) * mm, "end": v(7.03, -7.43) * mm});
            skLineSegment(sketch, "E350", {"start": v(7.03, -7.43) * mm, "end": v(7.14, -7.44) * mm});
            skLineSegment(sketch, "E351", {"start": v(7.14, -7.44) * mm, "end": v(7.33, -7.48) * mm});
            skLineSegment(sketch, "E352", {"start": v(7.33, -7.48) * mm, "end": v(7.51, -7.54) * mm});
            skLineSegment(sketch, "E353", {"start": v(7.51, -7.54) * mm, "end": v(7.77, -7.65) * mm});
            skLineSegment(sketch, "E354", {"start": v(7.77, -7.65) * mm, "end": v(8.08, -7.83) * mm});
            skLineSegment(sketch, "E355", {"start": v(8.08, -7.83) * mm, "end": v(8.48, -8.1) * mm});
            skLineSegment(sketch, "E356", {"start": v(8.48, -8.1) * mm, "end": v(8.82, -8.37) * mm});
            skLineSegment(sketch, "E357", {"start": v(8.82, -8.37) * mm, "end": v(9.06, -8.6) * mm});
            skLineSegment(sketch, "E358", {"start": v(9.06, -8.6) * mm, "end": v(9.35, -8.92) * mm});
            skLineSegment(sketch, "E359", {"start": v(9.35, -8.92) * mm, "end": v(9.7, -9.4) * mm});
            skLineSegment(sketch, "E360", {"start": v(9.7, -9.4) * mm, "end": v(10.07, -10.04) * mm});
            skLineSegment(sketch, "E361", {"start": v(10.07, -10.04) * mm, "end": v(10.5, -10.99) * mm});
            skLineSegment(sketch, "E362", {"start": v(10.5, -10.99) * mm, "end": v(10.95, -12.24) * mm});
            skLineSegment(sketch, "E363", {"start": v(10.95, -12.24) * mm, "end": v(11.22, -13.24) * mm});
            skLineSegment(sketch, "E364", {"start": v(11.22, -13.24) * mm, "end": v(11.43, -14.27) * mm});
            skLineSegment(sketch, "E365", {"start": v(11.43, -14.27) * mm, "end": v(11.53, -14.35) * mm});
            skLineSegment(sketch, "E366", {"start": v(11.53, -14.35) * mm, "end": v(11.65, -14.43) * mm});
            skLineSegment(sketch, "E367", {"start": v(11.65, -14.43) * mm, "end": v(11.84, -14.53) * mm});
            skLineSegment(sketch, "E368", {"start": v(11.84, -14.53) * mm, "end": v(12.2, -14.68) * mm});
            skLineSegment(sketch, "E369", {"start": v(12.2, -14.68) * mm, "end": v(12.62, -14.83) * mm});
            skLineSegment(sketch, "E370", {"start": v(12.62, -14.83) * mm, "end": v(13.04, -15.03) * mm});
            skLineSegment(sketch, "E371", {"start": v(13.04, -15.03) * mm, "end": v(13.07, -14.6) * mm});
            skLineSegment(sketch, "E372", {"start": v(13.07, -14.6) * mm, "end": v(13.05, -14.2) * mm});
            skLineSegment(sketch, "E373", {"start": v(13.05, -14.2) * mm, "end": v(12.99, -13.84) * mm});
            skLineSegment(sketch, "E374", {"start": v(12.99, -13.84) * mm, "end": v(12.9, -13.51) * mm});
            skLineSegment(sketch, "E375", {"start": v(12.9, -13.51) * mm, "end": v(12.76, -13.13) * mm});
            skLineSegment(sketch, "E376", {"start": v(12.76, -13.13) * mm, "end": v(12.05, -11.6) * mm});
            skLineSegment(sketch, "E377", {"start": v(12.05, -11.6) * mm, "end": v(12, -11.37) * mm});
            skLineSegment(sketch, "E378", {"start": v(12, -11.37) * mm, "end": v(11.94, -11.05) * mm});
            skLineSegment(sketch, "E379", {"start": v(11.94, -11.05) * mm, "end": v(11.92, -10.7) * mm});
            skLineSegment(sketch, "E380", {"start": v(11.92, -10.7) * mm, "end": v(11.94, -10.14) * mm});
            skLineSegment(sketch, "E381", {"start": v(11.94, -10.14) * mm, "end": v(12.01, -8.77) * mm});
            skLineSegment(sketch, "E382", {"start": v(12.01, -8.77) * mm, "end": v(12, -8.43) * mm});
            skLineSegment(sketch, "E383", {"start": v(12, -8.43) * mm, "end": v(11.94, -8) * mm});
            skLineSegment(sketch, "E384", {"start": v(11.94, -8) * mm, "end": v(10.7, -6.8) * mm});
            skLineSegment(sketch, "E385", {"start": v(10.7, -6.8) * mm, "end": v(10.44, -6.46) * mm});
            skLineSegment(sketch, "E386", {"start": v(10.44, -6.46) * mm, "end": v(10.31, -6.25) * mm});
            skLineSegment(sketch, "E387", {"start": v(10.31, -6.25) * mm, "end": v(10.2, -6.04) * mm});
            skLineSegment(sketch, "E388", {"start": v(10.2, -6.04) * mm, "end": v(10.13, -5.82) * mm});
            skLineSegment(sketch, "E389", {"start": v(10.13, -5.82) * mm, "end": v(10.1, -5.67) * mm});
            skLineSegment(sketch, "E390", {"start": v(10.1, -5.67) * mm, "end": v(10.08, -5.51) * mm});
            skLineSegment(sketch, "E391", {"start": v(10.08, -5.51) * mm, "end": v(10.07, -5.36) * mm});
            skLineSegment(sketch, "E392", {"start": v(10.07, -5.36) * mm, "end": v(10.09, -5.2) * mm});
            skLineSegment(sketch, "E393", {"start": v(10.09, -5.2) * mm, "end": v(10.12, -5.03) * mm});
            skLineSegment(sketch, "E394", {"start": v(10.12, -5.03) * mm, "end": v(10.17, -4.87) * mm});
            skLineSegment(sketch, "E395", {"start": v(10.17, -4.87) * mm, "end": v(10.24, -4.7) * mm});
            skLineSegment(sketch, "E396", {"start": v(10.24, -4.7) * mm, "end": v(10.34, -4.72) * mm});
            skLineSegment(sketch, "E397", {"start": v(10.34, -4.72) * mm, "end": v(10.42, -4.76) * mm});
            skLineSegment(sketch, "E398", {"start": v(10.42, -4.76) * mm, "end": v(10.5, -4.8) * mm});
            skLineSegment(sketch, "E399", {"start": v(10.5, -4.8) * mm, "end": v(10.59, -4.87) * mm});
            skLineSegment(sketch, "E400", {"start": v(10.59, -4.87) * mm, "end": v(10.7, -4.97) * mm});
            skLineSegment(sketch, "E401", {"start": v(10.7, -4.97) * mm, "end": v(10.8, -5.09) * mm});
            skLineSegment(sketch, "E402", {"start": v(10.8, -5.09) * mm, "end": v(10.96, -5.31) * mm});
            skLineSegment(sketch, "E403", {"start": v(10.96, -5.31) * mm, "end": v(11.45, -6.14) * mm});
            skLineSegment(sketch, "E404", {"start": v(11.45, -6.14) * mm, "end": v(11.5, -6.2) * mm});
            skLineSegment(sketch, "E405", {"start": v(11.5, -6.2) * mm, "end": v(11.55, -6.24) * mm});
            skLineSegment(sketch, "E406", {"start": v(11.55, -6.24) * mm, "end": v(11.6, -6.28) * mm});
            skLineSegment(sketch, "E407", {"start": v(11.6, -6.28) * mm, "end": v(11.63, -6.3) * mm});
            skLineSegment(sketch, "E408", {"start": v(11.63, -6.3) * mm, "end": v(11.66, -6.3) * mm});
            skLineSegment(sketch, "E409", {"start": v(11.66, -6.3) * mm, "end": v(11.68, -6.3) * mm});
            skLineSegment(sketch, "E410", {"start": v(11.68, -6.3) * mm, "end": v(11.71, -6.31) * mm});
            skLineSegment(sketch, "E411", {"start": v(11.71, -6.31) * mm, "end": v(11.74, -6.31) * mm});
            skLineSegment(sketch, "E412", {"start": v(11.74, -6.31) * mm, "end": v(11.77, -6.3) * mm});
            skLineSegment(sketch, "E413", {"start": v(11.77, -6.3) * mm, "end": v(11.75, -6.3) * mm});
            skLineSegment(sketch, "E414", {"start": v(11.75, -6.3) * mm, "end": v(11.74, -6.3) * mm});
            skLineSegment(sketch, "E415", {"start": v(11.74, -6.3) * mm, "end": v(11.73, -6.3) * mm});
            skLineSegment(sketch, "E416", {"start": v(11.73, -6.3) * mm, "end": v(11.72, -6.29) * mm});
            skLineSegment(sketch, "E417", {"start": v(11.72, -6.29) * mm, "end": v(11.71, -6.28) * mm});
            skLineSegment(sketch, "E418", {"start": v(11.71, -6.28) * mm, "end": v(11.7, -6.27) * mm});
            skLineSegment(sketch, "E419", {"start": v(11.7, -6.27) * mm, "end": v(11.7, -6.26) * mm});
            skLineSegment(sketch, "E420", {"start": v(11.7, -6.26) * mm, "end": v(11.7, -6.25) * mm});
            skLineSegment(sketch, "E421", {"start": v(11.7, -6.25) * mm, "end": v(11.69, -6.23) * mm});
            skLineSegment(sketch, "E422", {"start": v(11.69, -6.23) * mm, "end": v(11.68, -6.2) * mm});
            skLineSegment(sketch, "E423", {"start": v(11.68, -6.2) * mm, "end": v(11.68, -6.1) * mm});
            skLineSegment(sketch, "E424", {"start": v(11.68, -6.1) * mm, "end": v(11.68, -5.97) * mm});
            skLineSegment(sketch, "E425", {"start": v(11.68, -5.97) * mm, "end": v(11.72, -6.03) * mm});
            skLineSegment(sketch, "E426", {"start": v(11.72, -6.03) * mm, "end": v(11.77, -6.08) * mm});
            skLineSegment(sketch, "E427", {"start": v(11.77, -6.08) * mm, "end": v(11.82, -6.13) * mm});
            skLineSegment(sketch, "E428", {"start": v(11.82, -6.13) * mm, "end": v(11.87, -6.17) * mm});
            skLineSegment(sketch, "E429", {"start": v(11.87, -6.17) * mm, "end": v(11.95, -6.22) * mm});
            skLineSegment(sketch, "E430", {"start": v(11.95, -6.22) * mm, "end": v(12.04, -6.26) * mm});
            skLineSegment(sketch, "E431", {"start": v(12.04, -6.26) * mm, "end": v(12.4, -6.38) * mm});
            skLineSegment(sketch, "E432", {"start": v(12.4, -6.38) * mm, "end": v(12.78, -6.48) * mm});
            skLineSegment(sketch, "E433", {"start": v(12.78, -6.48) * mm, "end": v(13.63, -6.7) * mm});
            skLineSegment(sketch, "E434", {"start": v(13.63, -6.7) * mm, "end": v(14.3, -6.8) * mm});
            skLineSegment(sketch, "E435", {"start": v(14.3, -6.8) * mm, "end": v(14.94, -6.84) * mm});
            skLineSegment(sketch, "E436", {"start": v(14.94, -6.84) * mm, "end": v(15.43, -6.82) * mm});
            skLineSegment(sketch, "E437", {"start": v(15.43, -6.82) * mm, "end": v(15.9, -6.76) * mm});
            skLineSegment(sketch, "E438", {"start": v(15.9, -6.76) * mm, "end": v(16.36, -6.66) * mm});
            skLineSegment(sketch, "E439", {"start": v(16.36, -6.66) * mm, "end": v(16.8, -6.52) * mm});
            skLineSegment(sketch, "E440", {"start": v(16.8, -6.52) * mm, "end": v(17.21, -6.34) * mm});
            skLineSegment(sketch, "E441", {"start": v(17.21, -6.34) * mm, "end": v(17.61, -6.11) * mm});
            skLineSegment(sketch, "E442", {"start": v(17.61, -6.11) * mm, "end": v(18, -5.85) * mm});
            skLineSegment(sketch, "E443", {"start": v(18, -5.85) * mm, "end": v(18.27, -5.62) * mm});
            skLineSegment(sketch, "E444", {"start": v(18.27, -5.62) * mm, "end": v(18.54, -5.38) * mm});
            skLineSegment(sketch, "E445", {"start": v(18.54, -5.38) * mm, "end": v(18.62, -5.3) * mm});
            skLineSegment(sketch, "E446", {"start": v(18.62, -5.3) * mm, "end": v(19.02, -4.99) * mm});
            skLineSegment(sketch, "E447", {"start": v(19.02, -4.99) * mm, "end": v(19.08, -4.92) * mm});
            skLineSegment(sketch, "E448", {"start": v(19.08, -4.92) * mm, "end": v(19.11, -4.87) * mm});
            skLineSegment(sketch, "E449", {"start": v(19.11, -4.87) * mm, "end": v(19.14, -4.83) * mm});
            skLineSegment(sketch, "E450", {"start": v(19.14, -4.83) * mm, "end": v(19.15, -4.8) * mm});
            skLineSegment(sketch, "E451", {"start": v(19.15, -4.8) * mm, "end": v(19.16, -4.76) * mm});
            skLineSegment(sketch, "E452", {"start": v(19.16, -4.76) * mm, "end": v(19.17, -4.72) * mm});
            skLineSegment(sketch, "E453", {"start": v(19.17, -4.72) * mm, "end": v(19.17, -4.68) * mm});
            skLineSegment(sketch, "E454", {"start": v(19.17, -4.68) * mm, "end": v(19.17, -4.64) * mm});
            skLineSegment(sketch, "E455", {"start": v(19.17, -4.64) * mm, "end": v(19.16, -4.6) * mm});
            skLineSegment(sketch, "E456", {"start": v(19.16, -4.6) * mm, "end": v(19.15, -4.57) * mm});
            skLineSegment(sketch, "E457", {"start": v(19.15, -4.57) * mm, "end": v(19.13, -4.53) * mm});
            skLineSegment(sketch, "E458", {"start": v(19.13, -4.53) * mm, "end": v(18.25, -4.8) * mm});
            skLineSegment(sketch, "E459", {"start": v(18.25, -4.8) * mm, "end": v(17.7, -4.9) * mm});
            skLineSegment(sketch, "E460", {"start": v(17.7, -4.9) * mm, "end": v(17.17, -4.94) * mm});
            skLineSegment(sketch, "E461", {"start": v(17.17, -4.94) * mm, "end": v(16.68, -4.93) * mm});
            skLineSegment(sketch, "E462", {"start": v(16.68, -4.93) * mm, "end": v(16.2, -4.87) * mm});
            skLineSegment(sketch, "E463", {"start": v(16.2, -4.87) * mm, "end": v(15.75, -4.75) * mm});
            skLineSegment(sketch, "E464", {"start": v(15.75, -4.75) * mm, "end": v(15.33, -4.6) * mm});
            skLineSegment(sketch, "E465", {"start": v(15.33, -4.6) * mm, "end": v(14.92, -4.4) * mm});
            skLineSegment(sketch, "E466", {"start": v(14.92, -4.4) * mm, "end": v(14.35, -4.05) * mm});
            skLineSegment(sketch, "E467", {"start": v(14.35, -4.05) * mm, "end": v(13.81, -3.63) * mm});
            skLineSegment(sketch, "E468", {"start": v(13.81, -3.63) * mm, "end": v(13.14, -2.99) * mm});
            skLineSegment(sketch, "E469", {"start": v(13.14, -2.99) * mm, "end": v(11.92, -1.55) * mm});
            skLineSegment(sketch, "E470", {"start": v(11.92, -1.55) * mm, "end": v(10.91, -0.3) * mm});
            skLineSegment(sketch, "E471", {"start": v(10.91, -0.3) * mm, "end": v(9.74, 0.89) * mm});
            skLineSegment(sketch, "E472", {"start": v(9.74, 0.89) * mm, "end": v(9.24, 1.25) * mm});
            skLineSegment(sketch, "E473", {"start": v(9.24, 1.25) * mm, "end": v(8.6, 1.65) * mm});
            skLineSegment(sketch, "E474", {"start": v(8.6, 1.65) * mm, "end": v(7.78, 2.04) * mm});
            skLineSegment(sketch, "E475", {"start": v(7.78, 2.04) * mm, "end": v(6.35, 2.57) * mm});
            skLineSegment(sketch, "E476", {"start": v(6.35, 2.57) * mm, "end": v(4.56, 3.13) * mm});
            skLineSegment(sketch, "E477", {"start": v(4.56, 3.13) * mm, "end": v(2.62, 3.85) * mm});
            skLineSegment(sketch, "E478", {"start": v(2.62, 3.85) * mm, "end": v(0.52, 4.9) * mm});
            skLineSegment(sketch, "E479", {"start": v(0.52, 4.9) * mm, "end": v(-1.08, 5.9) * mm});
            skLineSegment(sketch, "E480", {"start": v(-1.08, 5.9) * mm, "end": v(-2.22, 6.78) * mm});
            skLineSegment(sketch, "E481", {"start": v(-2.22, 6.78) * mm, "end": v(-3.12, 7.62) * mm});
            skLineSegment(sketch, "E482", {"start": v(-3.12, 7.62) * mm, "end": v(-3.93, 8.54) * mm});
            skLineSegment(sketch, "E483", {"start": v(-3.93, 8.54) * mm, "end": v(-4.54, 9.37) * mm});
            skLineSegment(sketch, "E484", {"start": v(-4.54, 9.37) * mm, "end": v(-4.86, 9.9) * mm});
            skLineSegment(sketch, "E485", {"start": v(-4.86, 9.9) * mm, "end": v(-5.16, 10.46) * mm});
            skLineSegment(sketch, "E486", {"start": v(-5.16, 10.46) * mm, "end": v(-5.05, 10.45) * mm});
            skLineSegment(sketch, "E487", {"start": v(-5.05, 10.45) * mm, "end": v(-4.94, 10.45) * mm});
            skLineSegment(sketch, "E488", {"start": v(-4.94, 10.45) * mm, "end": v(-4.84, 10.47) * mm});
            skLineSegment(sketch, "E489", {"start": v(-4.84, 10.47) * mm, "end": v(-4.74, 10.5) * mm});
            skLineSegment(sketch, "E490", {"start": v(-4.74, 10.5) * mm, "end": v(-4.57, 10.55) * mm});
            skLineSegment(sketch, "E491", {"start": v(-4.57, 10.55) * mm, "end": v(-4.4, 10.63) * mm});
            skLineSegment(sketch, "E492", {"start": v(-4.4, 10.63) * mm, "end": v(-4.4, 10.67) * mm});
            skLineSegment(sketch, "E493", {"start": v(-4.4, 10.67) * mm, "end": v(-4.42, 10.72) * mm});
            skLineSegment(sketch, "E494", {"start": v(-4.42, 10.72) * mm, "end": v(-4.44, 10.76) * mm});
            skLineSegment(sketch, "E495", {"start": v(-4.44, 10.76) * mm, "end": v(-4.46, 10.8) * mm});
            skLineSegment(sketch, "E496", {"start": v(-4.46, 10.8) * mm, "end": v(-4.51, 10.87) * mm});
            skLineSegment(sketch, "E497", {"start": v(-4.51, 10.87) * mm, "end": v(-4.59, 10.96) * mm});
            skLineSegment(sketch, "E498", {"start": v(-4.59, 10.96) * mm, "end": v(-5.03, 11.34) * mm});
            skLineSegment(sketch, "E499", {"start": v(-5.03, 11.34) * mm, "end": v(-5.5, 11.73) * mm});
            skLineSegment(sketch, "E500", {"start": v(-5.5, 11.73) * mm, "end": v(-5.54, 12.06) * mm});
            skLineSegment(sketch, "E501", {"start": v(-5.54, 12.06) * mm, "end": v(-5.61, 12.37) * mm});
            skLineSegment(sketch, "E502", {"start": v(-5.61, 12.37) * mm, "end": v(-5.72, 12.66) * mm});
            skLineSegment(sketch, "E503", {"start": v(-5.72, 12.66) * mm, "end": v(-5.84, 12.93) * mm});
            skLineSegment(sketch, "E504", {"start": v(-5.84, 12.93) * mm, "end": v(-6.05, 13.27) * mm});
            skLineSegment(sketch, "E505", {"start": v(-6.05, 13.27) * mm, "end": v(-6.35, 13.66) * mm});
            skLineSegment(sketch, "E506", {"start": v(-6.35, 13.66) * mm, "end": v(-7.95, 15.44) * mm});
            skLineSegment(sketch, "E507", {"start": v(-7.95, 15.44) * mm, "end": v(-8.06, 15.61) * mm});
            skLineSegment(sketch, "E508", {"start": v(-8.06, 15.61) * mm, "end": v(-8.21, 15.88) * mm});
            skLineSegment(sketch, "E509", {"start": v(-8.21, 15.88) * mm, "end": v(-8.3, 16.06) * mm});
            skLineSegment(sketch, "E510", {"start": v(-8.3, 16.06) * mm, "end": v(-8.7, 17.13) * mm});
            skLineSegment(sketch, "E511", {"start": v(-8.7, 17.13) * mm, "end": v(-8.78, 17.27) * mm});
            skLineSegment(sketch, "E512", {"start": v(-8.78, 17.27) * mm, "end": v(-8.85, 17.36) * mm});
            skLineSegment(sketch, "E513", {"start": v(-8.85, 17.36) * mm, "end": v(-8.9, 17.42) * mm});
            skLineSegment(sketch, "E514", {"start": v(-8.9, 17.42) * mm, "end": v(-8.95, 17.46) * mm});
            skLineSegment(sketch, "E515", {"start": v(-8.95, 17.46) * mm, "end": v(-9, 17.5) * mm});
            skLineSegment(sketch, "E516", {"start": v(-9, 17.5) * mm, "end": v(-9.06, 17.53) * mm});
            skLineSegment(sketch, "E517", {"start": v(-9.06, 17.53) * mm, "end": v(-9.13, 17.55) * mm});
            skLineSegment(sketch, "E518", {"start": v(-9.13, 17.55) * mm, "end": v(-9.16, 17.56) * mm});
            skLineSegment(sketch, "E519", {"start": v(-9.16, 17.56) * mm, "end": v(-9.23, 17.57) * mm});
            skLineSegment(sketch, "E520", {"start": v(-9.23, 17.57) * mm, "end": v(-9.3, 17.57) * mm});
            skLineSegment(sketch, "E521", {"start": v(-9.3, 17.57) * mm, "end": v(-9.36, 17.56) * mm});
            skLineSegment(sketch, "E522", {"start": v(-9.36, 17.56) * mm, "end": v(-9.42, 17.53) * mm});
            skLineSegment(sketch, "E523", {"start": v(-9.42, 17.53) * mm, "end": v(-9.48, 17.5) * mm});
            skLineSegment(sketch, "E524", {"start": v(-9.48, 17.5) * mm, "end": v(-9.53, 17.47) * mm});
            skLineSegment(sketch, "E525", {"start": v(-9.53, 17.47) * mm, "end": v(-9.58, 17.43) * mm});
            skLineSegment(sketch, "E526", {"start": v(-9.58, 17.43) * mm, "end": v(-9.63, 17.38) * mm});
            skLineSegment(sketch, "E527", {"start": v(-9.63, 17.38) * mm, "end": v(-9.7, 17.3) * mm});
            skLineSegment(sketch, "E528", {"start": v(-9.7, 17.3) * mm, "end": v(-9.75, 17.21) * mm});
            skLineSegment(sketch, "E529", {"start": v(-9.75, 17.21) * mm, "end": v(-9.82, 17.08) * mm});
            skLineSegment(sketch, "E530", {"start": v(-9.82, 17.08) * mm, "end": v(-9.9, 16.87) * mm});
            skLineSegment(sketch, "E531", {"start": v(-9.9, 16.87) * mm, "end": v(-10, 16.5) * mm});
            skLineSegment(sketch, "E532", {"start": v(-10, 16.5) * mm, "end": v(-10.08, 16.21) * mm});
            skLineSegment(sketch, "E533", {"start": v(-10.08, 16.21) * mm, "end": v(-10.27, 16.23) * mm});
            skLineSegment(sketch, "E534", {"start": v(-10.27, 16.23) * mm, "end": v(-10.4, 16.22) * mm});
            skLineSegment(sketch, "E535", {"start": v(-10.4, 16.22) * mm, "end": v(-10.48, 16.21) * mm});
            skLineSegment(sketch, "E536", {"start": v(-10.48, 16.21) * mm, "end": v(-10.55, 16.2) * mm});
            skLineSegment(sketch, "E537", {"start": v(-10.55, 16.2) * mm, "end": v(-10.61, 16.18) * mm});
            skLineSegment(sketch, "E538", {"start": v(-10.61, 16.18) * mm, "end": v(-10.65, 16.16) * mm});
            skLineSegment(sketch, "E539", {"start": v(-10.65, 16.16) * mm, "end": v(-10.7, 16.14) * mm});
            skLineSegment(sketch, "E540", {"start": v(-10.7, 16.14) * mm, "end": v(-10.73, 16.11) * mm});
            skLineSegment(sketch, "E541", {"start": v(-10.73, 16.11) * mm, "end": v(-10.76, 16.09) * mm});
            skLineSegment(sketch, "E542", {"start": v(-10.76, 16.09) * mm, "end": v(-10.79, 16.05) * mm});
            skLineSegment(sketch, "E543", {"start": v(-10.79, 16.05) * mm, "end": v(-10.81, 16.02) * mm});
            skLineSegment(sketch, "E544", {"start": v(-10.81, 16.02) * mm, "end": v(-10.83, 15.99) * mm});
            skLineSegment(sketch, "E545", {"start": v(-10.83, 15.99) * mm, "end": v(-10.84, 15.96) * mm});
            skLineSegment(sketch, "E546", {"start": v(-10.84, 15.96) * mm, "end": v(-10.73, 15.69) * mm});
            skLineSegment(sketch, "E547", {"start": v(-10.73, 15.69) * mm, "end": v(-10.64, 15.4) * mm});
            skLineSegment(sketch, "E548", {"start": v(-10.64, 15.4) * mm, "end": v(-10.57, 14.99) * mm});
            skLineSegment(sketch, "E549", {"start": v(-10.57, 14.99) * mm, "end": v(-10.52, 14.44) * mm});
            skLineSegment(sketch, "E550", {"start": v(-10.52, 14.44) * mm, "end": v(-10.54, 13.53) * mm});
            skLineSegment(sketch, "E551", {"start": v(-10.54, 13.53) * mm, "end": v(-10.65, 12.06) * mm});
            skLineSegment(sketch, "E552", {"start": v(-10.65, 12.06) * mm, "end": v(-10.67, 10.71) * mm});
            skLineSegment(sketch, "E553", {"start": v(-10.67, 10.71) * mm, "end": v(-10.7, 10.7) * mm});
            skLineSegment(sketch, "E554", {"start": v(-10.7, 10.7) * mm, "end": v(-10.74, 10.7) * mm});
            skLineSegment(sketch, "E555", {"start": v(-10.74, 10.7) * mm, "end": v(-10.77, 10.7) * mm});
            skLineSegment(sketch, "E556", {"start": v(-10.77, 10.7) * mm, "end": v(-10.82, 10.7) * mm});
            skLineSegment(sketch, "E557", {"start": v(-10.82, 10.7) * mm, "end": v(-10.89, 10.71) * mm});
            skLineSegment(sketch, "E558", {"start": v(-10.89, 10.71) * mm, "end": v(-11.02, 10.76) * mm});
            skLineSegment(sketch, "E559", {"start": v(-11.02, 10.76) * mm, "end": v(-11.16, 10.8) * mm});
            skLineSegment(sketch, "E560", {"start": v(-11.16, 10.8) * mm, "end": v(-11.2, 10.8) * mm});
            skLineSegment(sketch, "E561", {"start": v(-11.2, 10.8) * mm, "end": v(-11.24, 10.8) * mm});
            skLineSegment(sketch, "E562", {"start": v(-11.24, 10.8) * mm, "end": v(-11.27, 10.8) * mm});
            skLineSegment(sketch, "E563", {"start": v(-11.27, 10.8) * mm, "end": v(-11.3, 10.8) * mm});
            skLineSegment(sketch, "E564", {"start": v(-11.3, 10.8) * mm, "end": v(-11.32, 10.8) * mm});
            skLineSegment(sketch, "E565", {"start": v(-11.32, 10.8) * mm, "end": v(-11.35, 10.79) * mm});
            skLineSegment(sketch, "E566", {"start": v(-11.35, 10.79) * mm, "end": v(-11.37, 10.77) * mm});
            skLineSegment(sketch, "E567", {"start": v(-11.37, 10.77) * mm, "end": v(-11.4, 10.75) * mm});
            skLineSegment(sketch, "E568", {"start": v(-11.4, 10.75) * mm, "end": v(-11.4, 10.74) * mm});
            skLineSegment(sketch, "E569", {"start": v(-11.4, 10.74) * mm, "end": v(-11.43, 10.71) * mm});
            skLineSegment(sketch, "E570", {"start": v(-11.43, 10.71) * mm, "end": v(-11.09, 10.48) * mm});
            skLineSegment(sketch, "E571", {"start": v(-11.09, 10.48) * mm, "end": v(-11.01, 10.42) * mm});
            skLineSegment(sketch, "E572", {"start": v(-11.01, 10.42) * mm, "end": v(-10.97, 10.37) * mm});
            skLineSegment(sketch, "E573", {"start": v(-10.97, 10.37) * mm, "end": v(-10.93, 10.31) * mm});
            skLineSegment(sketch, "E574", {"start": v(-10.93, 10.31) * mm, "end": v(-10.9, 10.25) * mm});
            skLineSegment(sketch, "E575", {"start": v(-10.9, 10.25) * mm, "end": v(-10.86, 10.19) * mm});
            skLineSegment(sketch, "E576", {"start": v(-10.86, 10.19) * mm, "end": v(-10.84, 10.12) * mm});
            skLineSegment(sketch, "E577", {"start": v(-10.84, 10.12) * mm, "end": v(-11, 10.05) * mm});
            skLineSegment(sketch, "E578", {"start": v(-11, 10.05) * mm, "end": v(-11.07, 10.01) * mm});
            skLineSegment(sketch, "E579", {"start": v(-11.07, 10.01) * mm, "end": v(-11.12, 9.98) * mm});
            skLineSegment(sketch, "E580", {"start": v(-11.12, 9.98) * mm, "end": v(-11.14, 9.96) * mm});
            skLineSegment(sketch, "E581", {"start": v(-11.14, 9.96) * mm, "end": v(-11.15, 9.94) * mm});
            skLineSegment(sketch, "E582", {"start": v(-11.15, 9.94) * mm, "end": v(-11.16, 9.93) * mm});
            skLineSegment(sketch, "E583", {"start": v(-11.16, 9.93) * mm, "end": v(-11.17, 9.92) * mm});
            skLineSegment(sketch, "E584", {"start": v(-11.17, 9.92) * mm, "end": v(-11.17, 9.9) * mm});
            skLineSegment(sketch, "E585", {"start": v(-11.17, 9.9) * mm, "end": v(-11.17, 9.9) * mm});
            skLineSegment(sketch, "E586", {"start": v(-11.17, 9.9) * mm, "end": v(-11.17, 9.89) * mm});
            skLineSegment(sketch, "E587", {"start": v(-11.17, 9.89) * mm, "end": v(-11.17, 9.88) * mm});
            skLineSegment(sketch, "E588", {"start": v(-11.17, 9.88) * mm, "end": v(-11.17, 9.87) * mm});
            skLineSegment(sketch, "E589", {"start": v(-11.17, 9.87) * mm, "end": v(-11.17, 9.84) * mm});
            skLineSegment(sketch, "E590", {"start": v(-11.17, 9.84) * mm, "end": v(-11.16, 9.82) * mm});
            skLineSegment(sketch, "E591", {"start": v(-11.16, 9.82) * mm, "end": v(-11.15, 9.8) * mm});
            skLineSegment(sketch, "E592", {"start": v(-11.15, 9.8) * mm, "end": v(-11.12, 9.75) * mm});
            skLineSegment(sketch, "E593", {"start": v(-11.12, 9.75) * mm, "end": v(-11.03, 9.62) * mm});
            skLineSegment(sketch, "E594", {"start": v(-11.03, 9.62) * mm, "end": v(-10.92, 9.44) * mm});
            skLineSegment(sketch, "E595", {"start": v(-10.92, 9.44) * mm, "end": v(-11.12, 8.4) * mm});
            skLineSegment(sketch, "E596", {"start": v(-11.12, 8.4) * mm, "end": v(-11.23, 7.32) * mm});
            skLineSegment(sketch, "E597", {"start": v(-11.23, 7.32) * mm, "end": v(-11.24, 6.19) * mm});
            skLineSegment(sketch, "E598", {"start": v(-11.24, 6.19) * mm, "end": v(-11.19, 5.44) * mm});
            skLineSegment(sketch, "E599", {"start": v(-11.19, 5.44) * mm, "end": v(-11.1, 4.61) * mm});
            skLineSegment(sketch, "E600", {"start": v(-11.1, 4.61) * mm, "end": v(-10.94, 3.8) * mm});
            skLineSegment(sketch, "E601", {"start": v(-10.94, 3.8) * mm, "end": v(-10.66, 2.82) * mm});
            skLineSegment(sketch, "E602", {"start": v(-10.66, 2.82) * mm, "end": v(-9.56, -0.42) * mm});
            skLineSegment(sketch, "E603", {"start": v(-9.56, -0.42) * mm, "end": v(-9.47, -0.93) * mm});
            skLineSegment(sketch, "E604", {"start": v(-9.47, -0.93) * mm, "end": v(-9.4, -1.48) * mm});
            skLineSegment(sketch, "E605", {"start": v(-9.4, -1.48) * mm, "end": v(-9.3, -0.87) * mm});
            skLineSegment(sketch, "E606", {"start": v(-9.3, -0.87) * mm, "end": v(-9.25, -0.71) * mm});
            skLineSegment(sketch, "E607", {"start": v(-9.25, -0.71) * mm, "end": v(-9.21, -0.62) * mm});
            skLineSegment(sketch, "E608", {"start": v(-9.21, -0.62) * mm, "end": v(-9.18, -0.55) * mm});
            skLineSegment(sketch, "E609", {"start": v(-9.18, -0.55) * mm, "end": v(-9.14, -0.49) * mm});
            skLineSegment(sketch, "E610", {"start": v(-9.14, -0.49) * mm, "end": v(-9.1, -0.43) * mm});
            skLineSegment(sketch, "E611", {"start": v(-9.1, -0.43) * mm, "end": v(-9.04, -0.38) * mm});
            skLineSegment(sketch, "E612", {"start": v(-9.04, -0.38) * mm, "end": v(-9, -0.35) * mm});
            skLineSegment(sketch, "E613", {"start": v(-9, -0.35) * mm, "end": v(-8.96, -0.33) * mm});
            skLineSegment(sketch, "E614", {"start": v(-8.96, -0.33) * mm, "end": v(-8.94, -0.32) * mm});
            skLineSegment(sketch, "E615", {"start": v(-8.94, -0.32) * mm, "end": v(-8.89, -0.3) * mm});
            skLineSegment(sketch, "E616", {"start": v(-8.89, -0.3) * mm, "end": v(-8.87, -0.33) * mm});
            skLineSegment(sketch, "E617", {"start": v(-8.87, -0.33) * mm, "end": v(-8.85, -0.37) * mm});
            skLineSegment(sketch, "E618", {"start": v(-8.85, -0.37) * mm, "end": v(-8.84, -0.43) * mm});
            skLineSegment(sketch, "E619", {"start": v(-8.84, -0.43) * mm, "end": v(-8.82, -0.5) * mm});
            skLineSegment(sketch, "E620", {"start": v(-8.82, -0.5) * mm, "end": v(-8.81, -0.62) * mm});
            skLineSegment(sketch, "E621", {"start": v(-8.81, -0.62) * mm, "end": v(-8.8, -1.26) * mm});
            skLineSegment(sketch, "E622", {"start": v(-8.8, -1.26) * mm, "end": v(-8.78, -1.35) * mm});
            skLineSegment(sketch, "E623", {"start": v(-8.78, -1.35) * mm, "end": v(-8.76, -1.41) * mm});
            skLineSegment(sketch, "E624", {"start": v(-8.76, -1.41) * mm, "end": v(-8.74, -1.45) * mm});
            skLineSegment(sketch, "E625", {"start": v(-8.74, -1.45) * mm, "end": v(-8.72, -1.48) * mm});
            skLineSegment(sketch, "E626", {"start": v(-8.72, -1.48) * mm, "end": v(-8.7, -1.49) * mm});
            skLineSegment(sketch, "E627", {"start": v(-8.7, -1.49) * mm, "end": v(-8.7, -1.5) * mm});
            skLineSegment(sketch, "E628", {"start": v(-8.7, -1.5) * mm, "end": v(-8.69, -1.5) * mm});
            skLineSegment(sketch, "E629", {"start": v(-8.69, -1.5) * mm, "end": v(-8.68, -1.5) * mm});
            skLineSegment(sketch, "E630", {"start": v(-8.68, -1.5) * mm, "end": v(-8.67, -1.5) * mm});
            skLineSegment(sketch, "E631", {"start": v(-8.67, -1.5) * mm, "end": v(-8.65, -1.5) * mm});
            skLineSegment(sketch, "E632", {"start": v(-8.65, -1.5) * mm, "end": v(-8.64, -1.49) * mm});
            skLineSegment(sketch, "E633", {"start": v(-8.64, -1.49) * mm, "end": v(-8.63, -1.48) * mm});
            skLineSegment(sketch, "E634", {"start": v(-8.63, -1.48) * mm, "end": v(-8.62, -1.48) * mm});
            skLineSegment(sketch, "E635", {"start": v(-8.62, -1.48) * mm, "end": v(-8.6, -1.45) * mm});
            skLineSegment(sketch, "E636", {"start": v(-8.6, -1.45) * mm, "end": v(-8.57, -1.42) * mm});
            skLineSegment(sketch, "E637", {"start": v(-8.57, -1.42) * mm, "end": v(-8.38, -1.16) * mm});
            skLineSegment(sketch, "E638", {"start": v(-8.38, -1.16) * mm, "end": v(-8.34, -1.12) * mm});
            skLineSegment(sketch, "E639", {"start": v(-8.34, -1.12) * mm, "end": v(-8.3, -1.1) * mm});
            skLineSegment(sketch, "E640", {"start": v(-8.3, -1.1) * mm, "end": v(-8.27, -1.07) * mm});
            skLineSegment(sketch, "E641", {"start": v(-8.27, -1.07) * mm, "end": v(-8.23, -1.06) * mm});
            skLineSegment(sketch, "E642", {"start": v(-8.23, -1.06) * mm, "end": v(-8.21, -1.05) * mm});
            skLineSegment(sketch, "E643", {"start": v(-8.21, -1.05) * mm, "end": v(-8.2, -1.05) * mm});
            skLineSegment(sketch, "E644", {"start": v(-8.2, -1.05) * mm, "end": v(-8.17, -1.05) * mm});
            skLineSegment(sketch, "E645", {"start": v(-8.17, -1.05) * mm, "end": v(-8.15, -1.05) * mm});
            skLineSegment(sketch, "E646", {"start": v(-8.15, -1.05) * mm, "end": v(-8.13, -1.05) * mm});
            skLineSegment(sketch, "E647", {"start": v(-8.13, -1.05) * mm, "end": v(-8.1, -1.06) * mm});
            skLineSegment(sketch, "E648", {"start": v(-8.1, -1.06) * mm, "end": v(-8.06, -1.08) * mm});
            skLineSegment(sketch, "E649", {"start": v(-8.06, -1.08) * mm, "end": v(-8.01, -1.1) * mm});
            skLineSegment(sketch, "E650", {"start": v(-8.01, -1.1) * mm, "end": v(-7.96, -1.14) * mm});
            skLineSegment(sketch, "E651", {"start": v(-7.96, -1.14) * mm, "end": v(-8.01, -1.37) * mm});
            skLineSegment(sketch, "E652", {"start": v(-8.01, -1.37) * mm, "end": v(-8.04, -1.58) * mm});
            skLineSegment(sketch, "E653", {"start": v(-8.04, -1.58) * mm, "end": v(-8.05, -1.78) * mm});
            skLineSegment(sketch, "E654", {"start": v(-8.05, -1.78) * mm, "end": v(-8.03, -1.96) * mm});
            skLineSegment(sketch, "E655", {"start": v(-8.03, -1.96) * mm, "end": v(-8, -2.14) * mm});
            skLineSegment(sketch, "E656", {"start": v(-8, -2.14) * mm, "end": v(-7.94, -2.3) * mm});
            skLineSegment(sketch, "E657", {"start": v(-7.94, -2.3) * mm, "end": v(-7.85, -2.52) * mm});
            skLineSegment(sketch, "E658", {"start": v(-7.85, -2.52) * mm, "end": v(-7.7, -2.76) * mm});
            skLineSegment(sketch, "E659", {"start": v(-7.7, -2.76) * mm, "end": v(-7.35, -3.25) * mm});
            skLineSegment(sketch, "E660", {"start": v(-7.35, -3.25) * mm, "end": v(-7.03, -3.77) * mm});
            skLineSegment(sketch, "E661", {"start": v(-7.03, -3.77) * mm, "end": v(-6.93, -4) * mm});
            skLineSegment(sketch, "E662", {"start": v(-6.93, -4) * mm, "end": v(-6.86, -4.25) * mm});
            skLineSegment(sketch, "E663", {"start": v(-6.86, -4.25) * mm, "end": v(-6.8, -4.58) * mm});
            skLineSegment(sketch, "E664", {"start": v(-6.8, -4.58) * mm, "end": v(-6.77, -5) * mm});
            skLineSegment(sketch, "E665", {"start": v(-6.77, -5) * mm, "end": v(-6.78, -5.64) * mm});
            skLineSegment(sketch, "E666", {"start": v(-6.78, -5.64) * mm, "end": v(-6.9, -7.01) * mm});
            skLineSegment(sketch, "E667", {"start": v(-6.9, -7.01) * mm, "end": v(-6.94, -8.5) * mm});
            skLineSegment(sketch, "E668", {"start": v(-6.94, -8.5) * mm, "end": v(-7.56, -8.37) * mm});
            skLineSegment(sketch, "E669", {"start": v(-7.56, -8.37) * mm, "end": v(-8.12, -8.31) * mm});
            skLineSegment(sketch, "E670", {"start": v(-8.12, -8.31) * mm, "end": v(-8.47, -8.31) * mm});
            skLineSegment(sketch, "E671", {"start": v(-8.47, -8.31) * mm, "end": v(-8.8, -8.34) * mm});
            skLineSegment(sketch, "E672", {"start": v(-8.8, -8.34) * mm, "end": v(-9.27, -8.44) * mm});
            skLineSegment(sketch, "E673", {"start": v(-9.27, -8.44) * mm, "end": v(-9.7, -8.58) * mm});
            skLineSegment(sketch, "E674", {"start": v(-9.7, -8.58) * mm, "end": v(-10.1, -8.76) * mm});
            skLineSegment(sketch, "E675", {"start": v(-10.1, -8.76) * mm, "end": v(-10.75, -9.12) * mm});
            skLineSegment(sketch, "E676", {"start": v(-10.75, -9.12) * mm, "end": v(-12.29, -10.04) * mm});
            skLineSegment(sketch, "E677", {"start": v(-12.29, -10.04) * mm, "end": v(-12.86, -10.29) * mm});
            skLineSegment(sketch, "E678", {"start": v(-12.86, -10.29) * mm, "end": v(-13.32, -10.43) * mm});
            skLineSegment(sketch, "E679", {"start": v(-13.32, -10.43) * mm, "end": v(-13.82, -10.52) * mm});
            skLineSegment(sketch, "E680", {"start": v(-13.82, -10.52) * mm, "end": v(-14.18, -10.54) * mm});
            skLineSegment(sketch, "E681", {"start": v(-14.18, -10.54) * mm, "end": v(-14.56, -10.54) * mm});
            skLineSegment(sketch, "E682", {"start": v(-14.56, -10.54) * mm, "end": v(-16.22, -11.8) * mm});
            skLineSegment(sketch, "E683", {"start": v(-16.22, -11.8) * mm, "end": v(-16.52, -12.12) * mm});
            skLineSegment(sketch, "E684", {"start": v(-16.52, -12.12) * mm, "end": v(-16.73, -12.4) * mm});
            skLineSegment(sketch, "E685", {"start": v(-16.73, -12.4) * mm, "end": v(-16.86, -12.62) * mm});
            skLineSegment(sketch, "E686", {"start": v(-16.86, -12.62) * mm, "end": v(-16.97, -12.86) * mm});
            skLineSegment(sketch, "E687", {"start": v(-16.97, -12.86) * mm, "end": v(-17.05, -13.1) * mm});
            skLineSegment(sketch, "E688", {"start": v(-17.05, -13.1) * mm, "end": v(-17.1, -13.38) * mm});
            skLineSegment(sketch, "E689", {"start": v(-17.1, -13.38) * mm, "end": v(-17.1, -13.56) * mm});
            skLineSegment(sketch, "E690", {"start": v(-17.1, -13.56) * mm, "end": v(-17.1, -13.76) * mm});
            skLineSegment(sketch, "E691", {"start": v(-17.1, -13.76) * mm, "end": v(-17.1, -13.85) * mm});
            skLineSegment(sketch, "E692", {"start": v(-17.1, -13.85) * mm, "end": v(-17.07, -13.93) * mm});
            skLineSegment(sketch, "E693", {"start": v(-17.07, -13.93) * mm, "end": v(-17.05, -14.01) * mm});
            skLineSegment(sketch, "E694", {"start": v(-17.05, -14.01) * mm, "end": v(-17.01, -14.1) * mm});
            skLineSegment(sketch, "E695", {"start": v(-17.01, -14.1) * mm, "end": v(-16.95, -14.2) * mm});
            skLineSegment(sketch, "E696", {"start": v(-16.95, -14.2) * mm, "end": v(-16.87, -14.31) * mm});
            skLineSegment(sketch, "E697", {"start": v(-16.87, -14.31) * mm, "end": v(-16.73, -14.48) * mm});
            skLineSegment(sketch, "E698", {"start": v(-16.73, -14.48) * mm, "end": v(-16.16, -15.06) * mm});
            skLineSegment(sketch, "E699", {"start": v(-16.16, -15.06) * mm, "end": v(-16.1, -15.15) * mm});
            skLineSegment(sketch, "E700", {"start": v(-16.1, -15.15) * mm, "end": v(-16.06, -15.22) * mm});
            skLineSegment(sketch, "E701", {"start": v(-16.06, -15.22) * mm, "end": v(-16.03, -15.28) * mm});
            skLineSegment(sketch, "E702", {"start": v(-16.03, -15.28) * mm, "end": v(-16.01, -15.35) * mm});
            skLineSegment(sketch, "E703", {"start": v(-16.01, -15.35) * mm, "end": v(-16, -15.38) * mm});
            skLineSegment(sketch, "E704", {"start": v(-16, -15.38) * mm, "end": v(-16, -15.45) * mm});
            skLineSegment(sketch, "E705", {"start": v(-16, -15.45) * mm, "end": v(-16.01, -15.57) * mm});
            skLineSegment(sketch, "E706", {"start": v(-16.01, -15.57) * mm, "end": v(-16.04, -15.69) * mm});
            skLineSegment(sketch, "E707", {"start": v(-16.04, -15.69) * mm, "end": v(-16.08, -15.8) * mm});
            skLineSegment(sketch, "E708", {"start": v(-16.08, -15.8) * mm, "end": v(-16.14, -15.9) * mm});
            skLineSegment(sketch, "E709", {"start": v(-16.14, -15.9) * mm, "end": v(-16.22, -16) * mm});
            skLineSegment(sketch, "E710", {"start": v(-16.22, -16) * mm, "end": v(-16.35, -16.15) * mm});
            skLineSegment(sketch, "E711", {"start": v(-16.35, -16.15) * mm, "end": v(-16.56, -16.33) * mm});
            skLineSegment(sketch, "E712", {"start": v(-16.56, -16.33) * mm, "end": v(-17.66, -17.14) * mm});
            skLineSegment(sketch, "E713", {"start": v(-17.66, -17.14) * mm, "end": v(-17.8, -17.3) * mm});
            skLineSegment(sketch, "E714", {"start": v(-17.8, -17.3) * mm, "end": v(-17.9, -17.4) * mm});
            skLineSegment(sketch, "E715", {"start": v(-17.9, -17.4) * mm, "end": v(-17.97, -17.53) * mm});
            skLineSegment(sketch, "E716", {"start": v(-17.97, -17.53) * mm, "end": v(-18.03, -17.65) * mm});
            skLineSegment(sketch, "E717", {"start": v(-18.03, -17.65) * mm, "end": v(-18.08, -17.79) * mm});
            skLineSegment(sketch, "E718", {"start": v(-18.08, -17.79) * mm, "end": v(-18.1, -17.93) * mm});
            skLineSegment(sketch, "E719", {"start": v(-18.1, -17.93) * mm, "end": v(-18.12, -18.08) * mm});
            skLineSegment(sketch, "E720", {"start": v(-18.12, -18.08) * mm, "end": v(-18.12, -18.15) * mm});
            skLineSegment(sketch, "E721", {"start": v(-18.12, -18.15) * mm, "end": v(-18.1, -18.21) * mm});
            skLineSegment(sketch, "E722", {"start": v(-18.1, -18.21) * mm, "end": v(-18.08, -18.31) * mm});
            skLineSegment(sketch, "E723", {"start": v(-18.08, -18.31) * mm, "end": v(-18.05, -18.4) * mm});
            skLineSegment(sketch, "E724", {"start": v(-18.05, -18.4) * mm, "end": v(-17.98, -18.53) * mm});
            skLineSegment(sketch, "E725", {"start": v(-17.98, -18.53) * mm, "end": v(-17.87, -18.7) * mm});
            skLineSegment(sketch, "E726", {"start": v(-17.87, -18.7) * mm, "end": v(-17.52, -19.19) * mm});
            skLineSegment(sketch, "E727", {"start": v(-17.52, -19.19) * mm, "end": v(-17.46, -19.32) * mm});
            skLineSegment(sketch, "E728", {"start": v(-17.46, -19.32) * mm, "end": v(-17.41, -19.42) * mm});
            skLineSegment(sketch, "E729", {"start": v(-17.41, -19.42) * mm, "end": v(-17.38, -19.53) * mm});
            skLineSegment(sketch, "E730", {"start": v(-17.38, -19.53) * mm, "end": v(-17.37, -19.6) * mm});
            skLineSegment(sketch, "E731", {"start": v(-17.37, -19.6) * mm, "end": v(-17.36, -19.69) * mm});
            skLineSegment(sketch, "E732", {"start": v(-17.36, -19.69) * mm, "end": v(-17.35, -19.79) * mm});
            skLineSegment(sketch, "E733", {"start": v(-17.35, -19.79) * mm, "end": v(-17.36, -19.92) * mm});
            skLineSegment(sketch, "E734", {"start": v(-17.36, -19.92) * mm, "end": v(-17.4, -20.1) * mm});
            skLineSegment(sketch, "E735", {"start": v(-17.4, -20.1) * mm, "end": v(-17.63, -21.02) * mm});
            skLineSegment(sketch, "E736", {"start": v(-17.63, -21.02) * mm, "end": v(-17.63, -21.13) * mm});
            skLineSegment(sketch, "E737", {"start": v(-17.63, -21.13) * mm, "end": v(-17.63, -21.22) * mm});
            skLineSegment(sketch, "E738", {"start": v(-17.63, -21.22) * mm, "end": v(-17.62, -21.24) * mm});
            skLineSegment(sketch, "E739", {"start": v(-17.62, -21.24) * mm, "end": v(-17.61, -21.3) * mm});
            skLineSegment(sketch, "E740", {"start": v(-17.61, -21.3) * mm, "end": v(-17.57, -21.42) * mm});
            skLineSegment(sketch, "E741", {"start": v(-17.57, -21.42) * mm, "end": v(-17.51, -21.55) * mm});
            skLineSegment(sketch, "E742", {"start": v(-17.51, -21.55) * mm, "end": v(-17.45, -21.66) * mm});
            skLineSegment(sketch, "E743", {"start": v(-17.45, -21.66) * mm, "end": v(-17.33, -21.83) * mm});
            skLineSegment(sketch, "E744", {"start": v(-17.33, -21.83) * mm, "end": v(-17.2, -21.98) * mm});
            skLineSegment(sketch, "E745", {"start": v(-17.2, -21.98) * mm, "end": v(-17.04, -22.12) * mm});
            skLineSegment(sketch, "E746", {"start": v(-17.04, -22.12) * mm, "end": v(-16.81, -22.3) * mm});
            skLineSegment(sketch, "E747", {"start": v(-16.81, -22.3) * mm, "end": v(-15.8, -22.88) * mm});
            skLineSegment(sketch, "E748", {"start": v(-15.8, -22.88) * mm, "end": v(-14.73, -23.5) * mm});
            skLineSegment(sketch, "E749", {"start": v(-14.73, -23.5) * mm, "end": v(-14.51, -23.67) * mm});
            skLineSegment(sketch, "E750", {"start": v(-14.51, -23.67) * mm, "end": v(-14.28, -23.9) * mm});
            skLineSegment(sketch, "E751", {"start": v(-14.28, -23.9) * mm, "end": v(-13.3, -24.99) * mm});
            skLineSegment(sketch, "E752", {"start": v(-13.3, -24.99) * mm, "end": v(-13.14, -25.11) * mm});
            skLineSegment(sketch, "E753", {"start": v(-13.14, -25.11) * mm, "end": v(-13, -25.2) * mm});
            skLineSegment(sketch, "E754", {"start": v(-13, -25.2) * mm, "end": v(-12.87, -25.27) * mm});
            skLineSegment(sketch, "E755", {"start": v(-12.87, -25.27) * mm, "end": v(24.47, -25.27) * mm});
            skLineSegment(sketch, "E756", {"start": v(24.47, -25.27) * mm, "end": v(24.6, -25.21) * mm});
            skLineSegment(sketch, "E757", {"start": v(24.6, -25.21) * mm, "end": v(24.73, -25.15) * mm});
            skLineSegment(sketch, "E758", {"start": v(24.73, -25.15) * mm, "end": v(24.84, -25.07) * mm});
            skLineSegment(sketch, "E759", {"start": v(24.84, -25.07) * mm, "end": v(24.95, -24.97) * mm});
            skLineSegment(sketch, "E760", {"start": v(24.95, -24.97) * mm, "end": v(25.05, -24.88) * mm});
            skLineSegment(sketch, "E761", {"start": v(25.05, -24.88) * mm, "end": v(25.15, -24.74) * mm});
            skLineSegment(sketch, "E762", {"start": v(25.15, -24.74) * mm, "end": v(25.24, -24.6) * mm});
            skLineSegment(sketch, "E763", {"start": v(25.24, -24.6) * mm, "end": v(25.32, -24.45) * mm});
            skLineSegment(sketch, "E764", {"start": v(25.32, -24.45) * mm, "end": v(25.4, -24.26) * mm});
            skLineSegment(sketch, "E765", {"start": v(25.4, -24.26) * mm, "end": v(25.4, 24.26) * mm});
            skLineSegment(sketch, "E766", {"start": v(25.4, 24.26) * mm, "end": v(25.3, 24.47) * mm});
            skLineSegment(sketch, "E767", {"start": v(25.3, 24.47) * mm, "end": v(25.21, 24.65) * mm});
            skLineSegment(sketch, "E768", {"start": v(25.21, 24.65) * mm, "end": v(25.12, 24.79) * mm});
            skLineSegment(sketch, "E769", {"start": v(25.12, 24.79) * mm, "end": v(25.03, 24.9) * mm});
            skLineSegment(sketch, "E770", {"start": v(25.03, 24.9) * mm, "end": v(24.93, 25) * mm});
            skLineSegment(sketch, "E771", {"start": v(24.93, 25) * mm, "end": v(24.82, 25.08) * mm});
            skLineSegment(sketch, "E772", {"start": v(24.82, 25.08) * mm, "end": v(24.7, 25.16) * mm});
            skLineSegment(sketch, "E773", {"start": v(24.7, 25.16) * mm, "end": v(24.6, 25.21) * mm});
            skLineSegment(sketch, "E774", {"start": v(24.6, 25.21) * mm, "end": v(24.47, 25.27) * mm});
            skLineSegment(sketch, "E775", {"start": v(24.47, 25.27) * mm, "end": v(-24.47, 25.27) * mm});
            skLineSegment(sketch, "E776", {"start": v(-24.47, 25.27) * mm, "end": v(-24.6, 25.21) * mm});
            skLineSegment(sketch, "E777", {"start": v(-24.6, 25.21) * mm, "end": v(-24.73, 25.14) * mm});
            skLineSegment(sketch, "E778", {"start": v(-24.73, 25.14) * mm, "end": v(-24.84, 25.06) * mm});
            skLineSegment(sketch, "E779", {"start": v(-24.84, 25.06) * mm, "end": v(-24.95, 24.97) * mm});
            skLineSegment(sketch, "E780", {"start": v(-24.95, 24.97) * mm, "end": v(-25.05, 24.88) * mm});
            skLineSegment(sketch, "E781", {"start": v(-25.05, 24.88) * mm, "end": v(-25.15, 24.74) * mm});
            skLineSegment(sketch, "E782", {"start": v(-25.15, 24.74) * mm, "end": v(-25.24, 24.6) * mm});
            skLineSegment(sketch, "E783", {"start": v(-25.24, 24.6) * mm, "end": v(-25.32, 24.45) * mm});
            skLineSegment(sketch, "E784", {"start": v(-25.32, 24.45) * mm, "end": v(-25.4, 24.26) * mm});
            skLineSegment(sketch, "E785", {"start": v(-25.4, 24.26) * mm, "end": v(-25.4, -24.26) * mm});
            skLineSegment(sketch, "E786", {"start": v(-17.4, -14.42) * mm, "end": v(-17.01, -14.1) * mm});
            skLineSegment(sketch, "E787", {"start": v(14.22, -15.6) * mm, "end": v(14.74, -14.63) * mm});
            skSolve(sketch);
        }
        {
            var Q0;
            Q0=makeQuery(id+"F0.imprint","IMPRINT",FACE,{"disambiguationData":[TD([[makeQuery(id+"F0.imprint","IMPRINT",EDGE,{"derivedFrom":sQuery(id+"F0.wireOp",EDGE,"E63")}),-1.0]])]});
            extrude(context, id + "F1", {"entities" : qUnion([Q0]), "depth" : 1.59 * mm, "offsetDistance" : 25.4 * mm});
        }
    });
